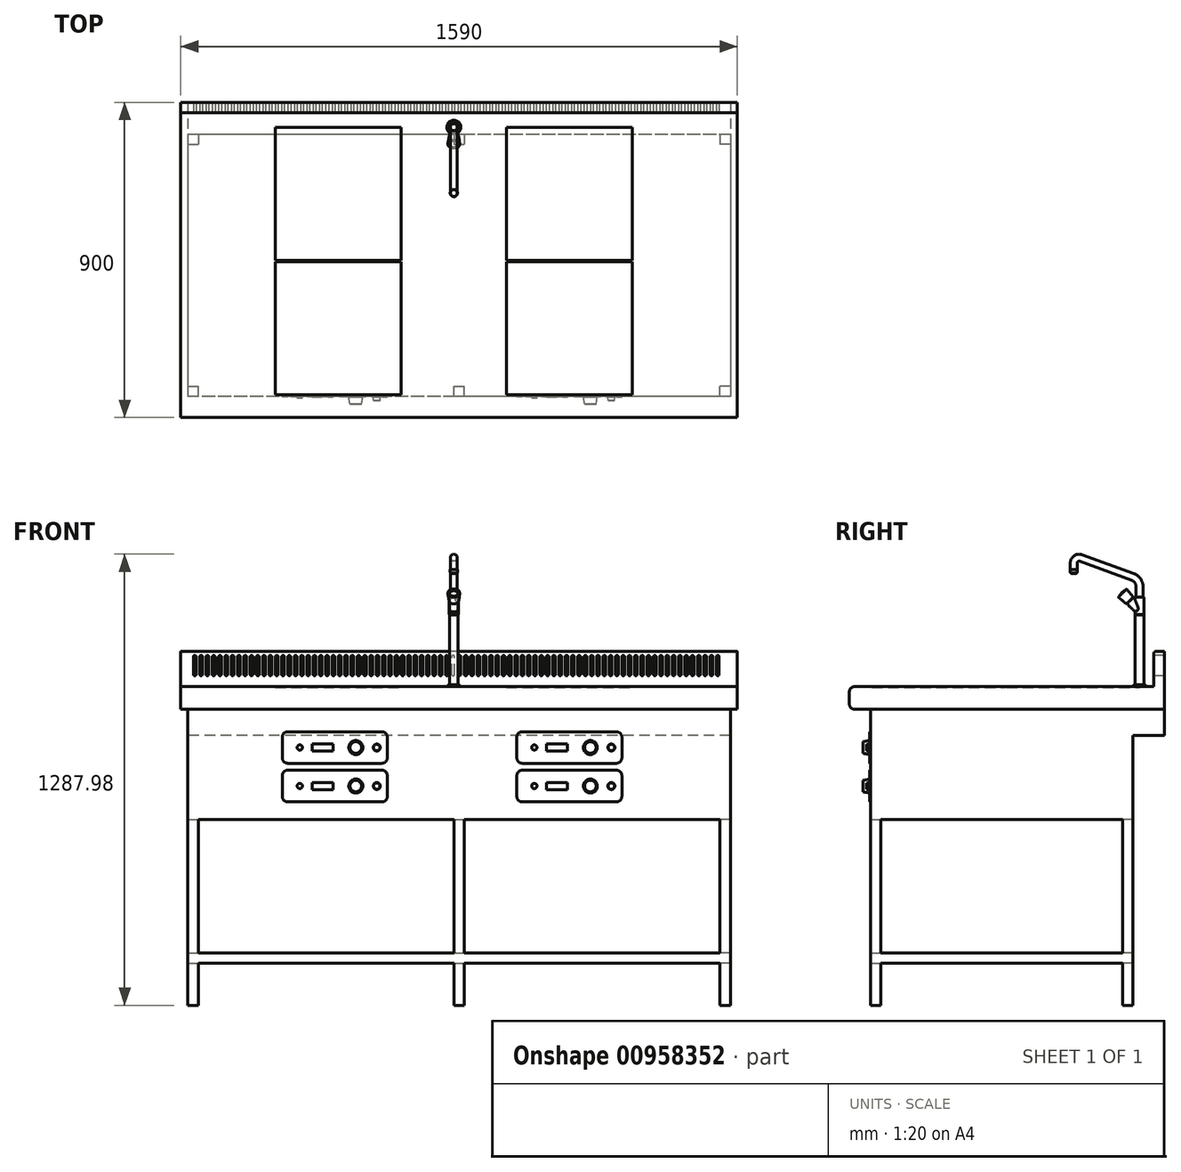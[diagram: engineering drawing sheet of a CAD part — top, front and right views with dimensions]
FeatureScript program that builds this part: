
annotation { "Feature Type Name" : "Feature", "Feature Type Description" : "" }
export const myFeature = defineFeature(function(context is Context, id is Id, definition is map)
    precondition{}
    {
        {
            var Q0;
            Q0=qCreatedBy(makeId("Right.planeOp"),FACE);
            var sketch = newSketch(context, id + "F0", { "sketchPlane" : qUnion([Q0])});
            skLineSegment(sketch, "E0", {"start": v(15, 0) * mm, "end": v(900, 0) * mm});
            skLineSegment(sketch, "E1", {"start": v(900, 0) * mm, "end": v(900, 165) * mm});
            skLineSegment(sketch, "E2", {"start": v(900, 165) * mm, "end": v(875, 165) * mm});
            skLineSegment(sketch, "E3", {"start": v(870, 160) * mm, "end": v(870, 65) * mm});
            skLineSegment(sketch, "E4", {"start": v(870, 65) * mm, "end": v(15, 65) * mm});
            skLineSegment(sketch, "E5", {"start": v(0, 50) * mm, "end": v(0, 15) * mm});
            skPoint(sketch, "E6.visualSharp", {"position": v(0, 65) * mm});
            skArc(sketch, "E6.filletArc", {"start": v(15, 65) * mm, "mid": v(4.4, 60.6) * mm, "end": v(0, 50) * mm});
            skPoint(sketch, "E7.visualSharp", {"position": v(0, 0) * mm});
            skArc(sketch, "E7.filletArc", {"start": v(0, 15) * mm, "mid": v(4.4, 4.4) * mm, "end": v(15, 0) * mm});
            skPoint(sketch, "E8.visualSharp", {"position": v(870, 165) * mm});
            skArc(sketch, "E8.filletArc", {"start": v(875, 165) * mm, "mid": v(871.46, 163.54) * mm, "end": v(870, 160) * mm});
            skPoint(sketch, "E9.visualSharp", {"position": v(900, 165) * mm});
            skSolve(sketch);
        }
        {
            var Q0;
            Q0 = qSketchRegion(id + "F0", true);
            extrude(context, id + "F1", {"entities" : qUnion([Q0]), "depth" : 1590 * mm, "offsetDistance" : 25 * mm});
        }
        {
            var Q0;
            Q0=makeQuery(id+"F1.opExtrude","SWEPT_FACE",FACE,{"disambiguationData":[OSD([sQuery(id+"F0.wireOp",EDGE,"E4")])]});
            var sketch = newSketch(context, id + "F2", { "sketchPlane" : qUnion([Q0])});
            skLineSegment(sketch, "E10.bottom", {"start": v(270, 65) * mm, "end": v(630, 65) * mm});
            skLineSegment(sketch, "E10.top", {"start": v(270, 445) * mm, "end": v(630, 445) * mm});
            skLineSegment(sketch, "E10.left", {"start": v(270, 65) * mm, "end": v(270, 445) * mm});
            skLineSegment(sketch, "E10.right", {"start": v(630, 65) * mm, "end": v(630, 445) * mm});
            skLineSegment(sketch, "E11.bottom", {"start": v(270, 449) * mm, "end": v(630, 449) * mm});
            skLineSegment(sketch, "E11.top", {"start": v(270, 829) * mm, "end": v(630, 829) * mm});
            skLineSegment(sketch, "E11.left", {"start": v(270, 449) * mm, "end": v(270, 829) * mm});
            skLineSegment(sketch, "E11.right", {"start": v(630, 449) * mm, "end": v(630, 829) * mm});
            skLineSegment(sketch, "E12.bottom", {"start": v(930, 65) * mm, "end": v(1290, 65) * mm});
            skLineSegment(sketch, "E12.top", {"start": v(930, 445) * mm, "end": v(1290, 445) * mm});
            skLineSegment(sketch, "E12.left", {"start": v(930, 65) * mm, "end": v(930, 445) * mm});
            skLineSegment(sketch, "E12.right", {"start": v(1290, 65) * mm, "end": v(1290, 445) * mm});
            skLineSegment(sketch, "E13.bottom", {"start": v(930, 449) * mm, "end": v(1290, 449) * mm});
            skLineSegment(sketch, "E13.top", {"start": v(930, 829) * mm, "end": v(1290, 829) * mm});
            skLineSegment(sketch, "E13.left", {"start": v(930, 449) * mm, "end": v(930, 829) * mm});
            skLineSegment(sketch, "E13.right", {"start": v(1290, 449) * mm, "end": v(1290, 829) * mm});
            skSolve(sketch);
        }
        {
            var Q0;
            Q0 = qSketchRegion(id + "F2", true);
            extrude(context, id + "F3", {"entities" : qUnion([Q0]), "operationType" : NewBodyOperationType.REMOVE, "oppositeDirection" : true, "depth" : 2 * mm, "offsetDistance" : 25 * mm});
        }
        {
            var Q0;
            Q0=makeQuery(id+"F1.opExtrude","SWEPT_FACE",FACE,{"disambiguationData":[OSD([sQuery(id+"F0.wireOp",EDGE,"E3")])]});
            var sketch = newSketch(context, id + "F4", { "sketchPlane" : qUnion([Q0])});
            skLineSegment(sketch, "E14", {"start": v(40, 150) * mm, "end": v(40, 100) * mm});
            skArc(sketch, "E15.0.startCap", {"start": v(36, 150) * mm, "mid": v(40, 154) * mm, "end": v(44, 150) * mm});
            skArc(sketch, "E15.0.endCap", {"start": v(44, 100) * mm, "mid": v(40, 96) * mm, "end": v(36, 100) * mm});
            skLineSegment(sketch, "E15.0.left", {"start": v(44, 150) * mm, "end": v(44, 100) * mm});
            skLineSegment(sketch, "E15.0.right", {"start": v(36, 150) * mm, "end": v(36, 100) * mm});
            skLineSegment(sketch, "E16.1.0.0", {"start": v(62, 150) * mm, "end": v(62, 100) * mm});
            skArc(sketch, "E16.1.0.1", {"start": v(54, 150) * mm, "mid": v(58, 154) * mm, "end": v(62, 150) * mm});
            skLineSegment(sketch, "E16.1.0.2", {"start": v(54, 150) * mm, "end": v(54, 100) * mm});
            skArc(sketch, "E16.1.0.3", {"start": v(62, 100) * mm, "mid": v(58, 96) * mm, "end": v(54, 100) * mm});
            skLineSegment(sketch, "E16.2.0.0", {"start": v(80, 150) * mm, "end": v(80, 100) * mm});
            skArc(sketch, "E16.2.0.1", {"start": v(72, 150) * mm, "mid": v(76, 154) * mm, "end": v(80, 150) * mm});
            skLineSegment(sketch, "E16.2.0.2", {"start": v(72, 150) * mm, "end": v(72, 100) * mm});
            skArc(sketch, "E16.2.0.3", {"start": v(80, 100) * mm, "mid": v(76, 96) * mm, "end": v(72, 100) * mm});
            skLineSegment(sketch, "E16.3.0.0", {"start": v(98, 150) * mm, "end": v(98, 100) * mm});
            skArc(sketch, "E16.3.0.1", {"start": v(90, 150) * mm, "mid": v(94, 154) * mm, "end": v(98, 150) * mm});
            skLineSegment(sketch, "E16.3.0.2", {"start": v(90, 150) * mm, "end": v(90, 100) * mm});
            skArc(sketch, "E16.3.0.3", {"start": v(98, 100) * mm, "mid": v(94, 96) * mm, "end": v(90, 100) * mm});
            skLineSegment(sketch, "E16.4.0.0", {"start": v(116, 150) * mm, "end": v(116, 100) * mm});
            skArc(sketch, "E16.4.0.1", {"start": v(108, 150) * mm, "mid": v(112, 154) * mm, "end": v(116, 150) * mm});
            skLineSegment(sketch, "E16.4.0.2", {"start": v(108, 150) * mm, "end": v(108, 100) * mm});
            skArc(sketch, "E16.4.0.3", {"start": v(116, 100) * mm, "mid": v(112, 96) * mm, "end": v(108, 100) * mm});
            skLineSegment(sketch, "E16.5.0.0", {"start": v(134, 150) * mm, "end": v(134, 100) * mm});
            skArc(sketch, "E16.5.0.1", {"start": v(126, 150) * mm, "mid": v(130, 154) * mm, "end": v(134, 150) * mm});
            skLineSegment(sketch, "E16.5.0.2", {"start": v(126, 150) * mm, "end": v(126, 100) * mm});
            skArc(sketch, "E16.5.0.3", {"start": v(134, 100) * mm, "mid": v(130, 96) * mm, "end": v(126, 100) * mm});
            skLineSegment(sketch, "E16.6.0.0", {"start": v(152, 150) * mm, "end": v(152, 100) * mm});
            skArc(sketch, "E16.6.0.1", {"start": v(144, 150) * mm, "mid": v(148, 154) * mm, "end": v(152, 150) * mm});
            skLineSegment(sketch, "E16.6.0.2", {"start": v(144, 150) * mm, "end": v(144, 100) * mm});
            skArc(sketch, "E16.6.0.3", {"start": v(152, 100) * mm, "mid": v(148, 96) * mm, "end": v(144, 100) * mm});
            skLineSegment(sketch, "E16.7.0.0", {"start": v(170, 150) * mm, "end": v(170, 100) * mm});
            skArc(sketch, "E16.7.0.1", {"start": v(162, 150) * mm, "mid": v(166, 154) * mm, "end": v(170, 150) * mm});
            skLineSegment(sketch, "E16.7.0.2", {"start": v(162, 150) * mm, "end": v(162, 100) * mm});
            skArc(sketch, "E16.7.0.3", {"start": v(170, 100) * mm, "mid": v(166, 96) * mm, "end": v(162, 100) * mm});
            skLineSegment(sketch, "E16.8.0.0", {"start": v(188, 150) * mm, "end": v(188, 100) * mm});
            skArc(sketch, "E16.8.0.1", {"start": v(180, 150) * mm, "mid": v(184, 154) * mm, "end": v(188, 150) * mm});
            skLineSegment(sketch, "E16.8.0.2", {"start": v(180, 150) * mm, "end": v(180, 100) * mm});
            skArc(sketch, "E16.8.0.3", {"start": v(188, 100) * mm, "mid": v(184, 96) * mm, "end": v(180, 100) * mm});
            skLineSegment(sketch, "E16.9.0.0", {"start": v(206, 150) * mm, "end": v(206, 100) * mm});
            skArc(sketch, "E16.9.0.1", {"start": v(198, 150) * mm, "mid": v(202, 154) * mm, "end": v(206, 150) * mm});
            skLineSegment(sketch, "E16.9.0.2", {"start": v(198, 150) * mm, "end": v(198, 100) * mm});
            skArc(sketch, "E16.9.0.3", {"start": v(206, 100) * mm, "mid": v(202, 96) * mm, "end": v(198, 100) * mm});
            skLineSegment(sketch, "E16.10.0.0", {"start": v(224, 150) * mm, "end": v(224, 100) * mm});
            skArc(sketch, "E16.10.0.1", {"start": v(216, 150) * mm, "mid": v(220, 154) * mm, "end": v(224, 150) * mm});
            skLineSegment(sketch, "E16.10.0.2", {"start": v(216, 150) * mm, "end": v(216, 100) * mm});
            skArc(sketch, "E16.10.0.3", {"start": v(224, 100) * mm, "mid": v(220, 96) * mm, "end": v(216, 100) * mm});
            skLineSegment(sketch, "E16.11.0.0", {"start": v(242, 150) * mm, "end": v(242, 100) * mm});
            skArc(sketch, "E16.11.0.1", {"start": v(234, 150) * mm, "mid": v(238, 154) * mm, "end": v(242, 150) * mm});
            skLineSegment(sketch, "E16.11.0.2", {"start": v(234, 150) * mm, "end": v(234, 100) * mm});
            skArc(sketch, "E16.11.0.3", {"start": v(242, 100) * mm, "mid": v(238, 96) * mm, "end": v(234, 100) * mm});
            skLineSegment(sketch, "E16.12.0.0", {"start": v(260, 150) * mm, "end": v(260, 100) * mm});
            skArc(sketch, "E16.12.0.1", {"start": v(252, 150) * mm, "mid": v(256, 154) * mm, "end": v(260, 150) * mm});
            skLineSegment(sketch, "E16.12.0.2", {"start": v(252, 150) * mm, "end": v(252, 100) * mm});
            skArc(sketch, "E16.12.0.3", {"start": v(260, 100) * mm, "mid": v(256, 96) * mm, "end": v(252, 100) * mm});
            skLineSegment(sketch, "E16.13.0.0", {"start": v(278, 150) * mm, "end": v(278, 100) * mm});
            skArc(sketch, "E16.13.0.1", {"start": v(270, 150) * mm, "mid": v(274, 154) * mm, "end": v(278, 150) * mm});
            skLineSegment(sketch, "E16.13.0.2", {"start": v(270, 150) * mm, "end": v(270, 100) * mm});
            skArc(sketch, "E16.13.0.3", {"start": v(278, 100) * mm, "mid": v(274, 96) * mm, "end": v(270, 100) * mm});
            skLineSegment(sketch, "E16.14.0.0", {"start": v(296, 150) * mm, "end": v(296, 100) * mm});
            skArc(sketch, "E16.14.0.1", {"start": v(288, 150) * mm, "mid": v(292, 154) * mm, "end": v(296, 150) * mm});
            skLineSegment(sketch, "E16.14.0.2", {"start": v(288, 150) * mm, "end": v(288, 100) * mm});
            skArc(sketch, "E16.14.0.3", {"start": v(296, 100) * mm, "mid": v(292, 96) * mm, "end": v(288, 100) * mm});
            skLineSegment(sketch, "E16.15.0.0", {"start": v(314, 150) * mm, "end": v(314, 100) * mm});
            skArc(sketch, "E16.15.0.1", {"start": v(306, 150) * mm, "mid": v(310, 154) * mm, "end": v(314, 150) * mm});
            skLineSegment(sketch, "E16.15.0.2", {"start": v(306, 150) * mm, "end": v(306, 100) * mm});
            skArc(sketch, "E16.15.0.3", {"start": v(314, 100) * mm, "mid": v(310, 96) * mm, "end": v(306, 100) * mm});
            skLineSegment(sketch, "E16.16.0.0", {"start": v(332, 150) * mm, "end": v(332, 100) * mm});
            skArc(sketch, "E16.16.0.1", {"start": v(324, 150) * mm, "mid": v(328, 154) * mm, "end": v(332, 150) * mm});
            skLineSegment(sketch, "E16.16.0.2", {"start": v(324, 150) * mm, "end": v(324, 100) * mm});
            skArc(sketch, "E16.16.0.3", {"start": v(332, 100) * mm, "mid": v(328, 96) * mm, "end": v(324, 100) * mm});
            skLineSegment(sketch, "E16.17.0.0", {"start": v(350, 150) * mm, "end": v(350, 100) * mm});
            skArc(sketch, "E16.17.0.1", {"start": v(342, 150) * mm, "mid": v(346, 154) * mm, "end": v(350, 150) * mm});
            skLineSegment(sketch, "E16.17.0.2", {"start": v(342, 150) * mm, "end": v(342, 100) * mm});
            skArc(sketch, "E16.17.0.3", {"start": v(350, 100) * mm, "mid": v(346, 96) * mm, "end": v(342, 100) * mm});
            skLineSegment(sketch, "E16.18.0.0", {"start": v(368, 150) * mm, "end": v(368, 100) * mm});
            skArc(sketch, "E16.18.0.1", {"start": v(360, 150) * mm, "mid": v(364, 154) * mm, "end": v(368, 150) * mm});
            skLineSegment(sketch, "E16.18.0.2", {"start": v(360, 150) * mm, "end": v(360, 100) * mm});
            skArc(sketch, "E16.18.0.3", {"start": v(368, 100) * mm, "mid": v(364, 96) * mm, "end": v(360, 100) * mm});
            skLineSegment(sketch, "E16.19.0.0", {"start": v(386, 150) * mm, "end": v(386, 100) * mm});
            skArc(sketch, "E16.19.0.1", {"start": v(378, 150) * mm, "mid": v(382, 154) * mm, "end": v(386, 150) * mm});
            skLineSegment(sketch, "E16.19.0.2", {"start": v(378, 150) * mm, "end": v(378, 100) * mm});
            skArc(sketch, "E16.19.0.3", {"start": v(386, 100) * mm, "mid": v(382, 96) * mm, "end": v(378, 100) * mm});
            skLineSegment(sketch, "E16.20.0.0", {"start": v(404, 150) * mm, "end": v(404, 100) * mm});
            skArc(sketch, "E16.20.0.1", {"start": v(396, 150) * mm, "mid": v(400, 154) * mm, "end": v(404, 150) * mm});
            skLineSegment(sketch, "E16.20.0.2", {"start": v(396, 150) * mm, "end": v(396, 100) * mm});
            skArc(sketch, "E16.20.0.3", {"start": v(404, 100) * mm, "mid": v(400, 96) * mm, "end": v(396, 100) * mm});
            skLineSegment(sketch, "E16.21.0.0", {"start": v(422, 150) * mm, "end": v(422, 100) * mm});
            skArc(sketch, "E16.21.0.1", {"start": v(414, 150) * mm, "mid": v(418, 154) * mm, "end": v(422, 150) * mm});
            skLineSegment(sketch, "E16.21.0.2", {"start": v(414, 150) * mm, "end": v(414, 100) * mm});
            skArc(sketch, "E16.21.0.3", {"start": v(422, 100) * mm, "mid": v(418, 96) * mm, "end": v(414, 100) * mm});
            skLineSegment(sketch, "E16.22.0.0", {"start": v(440, 150) * mm, "end": v(440, 100) * mm});
            skArc(sketch, "E16.22.0.1", {"start": v(432, 150) * mm, "mid": v(436, 154) * mm, "end": v(440, 150) * mm});
            skLineSegment(sketch, "E16.22.0.2", {"start": v(432, 150) * mm, "end": v(432, 100) * mm});
            skArc(sketch, "E16.22.0.3", {"start": v(440, 100) * mm, "mid": v(436, 96) * mm, "end": v(432, 100) * mm});
            skLineSegment(sketch, "E16.23.0.0", {"start": v(458, 150) * mm, "end": v(458, 100) * mm});
            skArc(sketch, "E16.23.0.1", {"start": v(450, 150) * mm, "mid": v(454, 154) * mm, "end": v(458, 150) * mm});
            skLineSegment(sketch, "E16.23.0.2", {"start": v(450, 150) * mm, "end": v(450, 100) * mm});
            skArc(sketch, "E16.23.0.3", {"start": v(458, 100) * mm, "mid": v(454, 96) * mm, "end": v(450, 100) * mm});
            skLineSegment(sketch, "E16.24.0.0", {"start": v(476, 150) * mm, "end": v(476, 100) * mm});
            skArc(sketch, "E16.24.0.1", {"start": v(468, 150) * mm, "mid": v(472, 154) * mm, "end": v(476, 150) * mm});
            skLineSegment(sketch, "E16.24.0.2", {"start": v(468, 150) * mm, "end": v(468, 100) * mm});
            skArc(sketch, "E16.24.0.3", {"start": v(476, 100) * mm, "mid": v(472, 96) * mm, "end": v(468, 100) * mm});
            skLineSegment(sketch, "E16.25.0.0", {"start": v(494, 150) * mm, "end": v(494, 100) * mm});
            skArc(sketch, "E16.25.0.1", {"start": v(486, 150) * mm, "mid": v(490, 154) * mm, "end": v(494, 150) * mm});
            skLineSegment(sketch, "E16.25.0.2", {"start": v(486, 150) * mm, "end": v(486, 100) * mm});
            skArc(sketch, "E16.25.0.3", {"start": v(494, 100) * mm, "mid": v(490, 96) * mm, "end": v(486, 100) * mm});
            skLineSegment(sketch, "E16.26.0.0", {"start": v(512, 150) * mm, "end": v(512, 100) * mm});
            skArc(sketch, "E16.26.0.1", {"start": v(504, 150) * mm, "mid": v(508, 154) * mm, "end": v(512, 150) * mm});
            skLineSegment(sketch, "E16.26.0.2", {"start": v(504, 150) * mm, "end": v(504, 100) * mm});
            skArc(sketch, "E16.26.0.3", {"start": v(512, 100) * mm, "mid": v(508, 96) * mm, "end": v(504, 100) * mm});
            skLineSegment(sketch, "E16.27.0.0", {"start": v(530, 150) * mm, "end": v(530, 100) * mm});
            skArc(sketch, "E16.27.0.1", {"start": v(522, 150) * mm, "mid": v(526, 154) * mm, "end": v(530, 150) * mm});
            skLineSegment(sketch, "E16.27.0.2", {"start": v(522, 150) * mm, "end": v(522, 100) * mm});
            skArc(sketch, "E16.27.0.3", {"start": v(530, 100) * mm, "mid": v(526, 96) * mm, "end": v(522, 100) * mm});
            skLineSegment(sketch, "E16.28.0.0", {"start": v(548, 150) * mm, "end": v(548, 100) * mm});
            skArc(sketch, "E16.28.0.1", {"start": v(540, 150) * mm, "mid": v(544, 154) * mm, "end": v(548, 150) * mm});
            skLineSegment(sketch, "E16.28.0.2", {"start": v(540, 150) * mm, "end": v(540, 100) * mm});
            skArc(sketch, "E16.28.0.3", {"start": v(548, 100) * mm, "mid": v(544, 96) * mm, "end": v(540, 100) * mm});
            skLineSegment(sketch, "E16.29.0.0", {"start": v(566, 150) * mm, "end": v(566, 100) * mm});
            skArc(sketch, "E16.29.0.1", {"start": v(558, 150) * mm, "mid": v(562, 154) * mm, "end": v(566, 150) * mm});
            skLineSegment(sketch, "E16.29.0.2", {"start": v(558, 150) * mm, "end": v(558, 100) * mm});
            skArc(sketch, "E16.29.0.3", {"start": v(566, 100) * mm, "mid": v(562, 96) * mm, "end": v(558, 100) * mm});
            skLineSegment(sketch, "E16.30.0.0", {"start": v(584, 150) * mm, "end": v(584, 100) * mm});
            skArc(sketch, "E16.30.0.1", {"start": v(576, 150) * mm, "mid": v(580, 154) * mm, "end": v(584, 150) * mm});
            skLineSegment(sketch, "E16.30.0.2", {"start": v(576, 150) * mm, "end": v(576, 100) * mm});
            skArc(sketch, "E16.30.0.3", {"start": v(584, 100) * mm, "mid": v(580, 96) * mm, "end": v(576, 100) * mm});
            skLineSegment(sketch, "E16.31.0.0", {"start": v(602, 150) * mm, "end": v(602, 100) * mm});
            skArc(sketch, "E16.31.0.1", {"start": v(594, 150) * mm, "mid": v(598, 154) * mm, "end": v(602, 150) * mm});
            skLineSegment(sketch, "E16.31.0.2", {"start": v(594, 150) * mm, "end": v(594, 100) * mm});
            skArc(sketch, "E16.31.0.3", {"start": v(602, 100) * mm, "mid": v(598, 96) * mm, "end": v(594, 100) * mm});
            skLineSegment(sketch, "E16.32.0.0", {"start": v(620, 150) * mm, "end": v(620, 100) * mm});
            skArc(sketch, "E16.32.0.1", {"start": v(612, 150) * mm, "mid": v(616, 154) * mm, "end": v(620, 150) * mm});
            skLineSegment(sketch, "E16.32.0.2", {"start": v(612, 150) * mm, "end": v(612, 100) * mm});
            skArc(sketch, "E16.32.0.3", {"start": v(620, 100) * mm, "mid": v(616, 96) * mm, "end": v(612, 100) * mm});
            skLineSegment(sketch, "E16.33.0.0", {"start": v(638, 150) * mm, "end": v(638, 100) * mm});
            skArc(sketch, "E16.33.0.1", {"start": v(630, 150) * mm, "mid": v(634, 154) * mm, "end": v(638, 150) * mm});
            skLineSegment(sketch, "E16.33.0.2", {"start": v(630, 150) * mm, "end": v(630, 100) * mm});
            skArc(sketch, "E16.33.0.3", {"start": v(638, 100) * mm, "mid": v(634, 96) * mm, "end": v(630, 100) * mm});
            skLineSegment(sketch, "E16.34.0.0", {"start": v(656, 150) * mm, "end": v(656, 100) * mm});
            skArc(sketch, "E16.34.0.1", {"start": v(648, 150) * mm, "mid": v(652, 154) * mm, "end": v(656, 150) * mm});
            skLineSegment(sketch, "E16.34.0.2", {"start": v(648, 150) * mm, "end": v(648, 100) * mm});
            skArc(sketch, "E16.34.0.3", {"start": v(656, 100) * mm, "mid": v(652, 96) * mm, "end": v(648, 100) * mm});
            skLineSegment(sketch, "E16.35.0.0", {"start": v(674, 150) * mm, "end": v(674, 100) * mm});
            skArc(sketch, "E16.35.0.1", {"start": v(666, 150) * mm, "mid": v(670, 154) * mm, "end": v(674, 150) * mm});
            skLineSegment(sketch, "E16.35.0.2", {"start": v(666, 150) * mm, "end": v(666, 100) * mm});
            skArc(sketch, "E16.35.0.3", {"start": v(674, 100) * mm, "mid": v(670, 96) * mm, "end": v(666, 100) * mm});
            skLineSegment(sketch, "E16.36.0.0", {"start": v(692, 150) * mm, "end": v(692, 100) * mm});
            skArc(sketch, "E16.36.0.1", {"start": v(684, 150) * mm, "mid": v(688, 154) * mm, "end": v(692, 150) * mm});
            skLineSegment(sketch, "E16.36.0.2", {"start": v(684, 150) * mm, "end": v(684, 100) * mm});
            skArc(sketch, "E16.36.0.3", {"start": v(692, 100) * mm, "mid": v(688, 96) * mm, "end": v(684, 100) * mm});
            skLineSegment(sketch, "E16.37.0.0", {"start": v(710, 150) * mm, "end": v(710, 100) * mm});
            skArc(sketch, "E16.37.0.1", {"start": v(702, 150) * mm, "mid": v(706, 154) * mm, "end": v(710, 150) * mm});
            skLineSegment(sketch, "E16.37.0.2", {"start": v(702, 150) * mm, "end": v(702, 100) * mm});
            skArc(sketch, "E16.37.0.3", {"start": v(710, 100) * mm, "mid": v(706, 96) * mm, "end": v(702, 100) * mm});
            skLineSegment(sketch, "E16.38.0.0", {"start": v(728, 150) * mm, "end": v(728, 100) * mm});
            skArc(sketch, "E16.38.0.1", {"start": v(720, 150) * mm, "mid": v(724, 154) * mm, "end": v(728, 150) * mm});
            skLineSegment(sketch, "E16.38.0.2", {"start": v(720, 150) * mm, "end": v(720, 100) * mm});
            skArc(sketch, "E16.38.0.3", {"start": v(728, 100) * mm, "mid": v(724, 96) * mm, "end": v(720, 100) * mm});
            skLineSegment(sketch, "E16.39.0.0", {"start": v(746, 150) * mm, "end": v(746, 100) * mm});
            skArc(sketch, "E16.39.0.1", {"start": v(738, 150) * mm, "mid": v(742, 154) * mm, "end": v(746, 150) * mm});
            skLineSegment(sketch, "E16.39.0.2", {"start": v(738, 150) * mm, "end": v(738, 100) * mm});
            skArc(sketch, "E16.39.0.3", {"start": v(746, 100) * mm, "mid": v(742, 96) * mm, "end": v(738, 100) * mm});
            skLineSegment(sketch, "E16.40.0.0", {"start": v(764, 150) * mm, "end": v(764, 100) * mm});
            skArc(sketch, "E16.40.0.1", {"start": v(756, 150) * mm, "mid": v(760, 154) * mm, "end": v(764, 150) * mm});
            skLineSegment(sketch, "E16.40.0.2", {"start": v(756, 150) * mm, "end": v(756, 100) * mm});
            skArc(sketch, "E16.40.0.3", {"start": v(764, 100) * mm, "mid": v(760, 96) * mm, "end": v(756, 100) * mm});
            skLineSegment(sketch, "E16.41.0.0", {"start": v(782, 150) * mm, "end": v(782, 100) * mm});
            skArc(sketch, "E16.41.0.1", {"start": v(774, 150) * mm, "mid": v(778, 154) * mm, "end": v(782, 150) * mm});
            skLineSegment(sketch, "E16.41.0.2", {"start": v(774, 150) * mm, "end": v(774, 100) * mm});
            skArc(sketch, "E16.41.0.3", {"start": v(782, 100) * mm, "mid": v(778, 96) * mm, "end": v(774, 100) * mm});
            skLineSegment(sketch, "E16.42.0.0", {"start": v(800, 150) * mm, "end": v(800, 100) * mm});
            skArc(sketch, "E16.42.0.1", {"start": v(792, 150) * mm, "mid": v(796, 154) * mm, "end": v(800, 150) * mm});
            skLineSegment(sketch, "E16.42.0.2", {"start": v(792, 150) * mm, "end": v(792, 100) * mm});
            skArc(sketch, "E16.42.0.3", {"start": v(800, 100) * mm, "mid": v(796, 96) * mm, "end": v(792, 100) * mm});
            skLineSegment(sketch, "E16.43.0.0", {"start": v(818, 150) * mm, "end": v(818, 100) * mm});
            skArc(sketch, "E16.43.0.1", {"start": v(810, 150) * mm, "mid": v(814, 154) * mm, "end": v(818, 150) * mm});
            skLineSegment(sketch, "E16.43.0.2", {"start": v(810, 150) * mm, "end": v(810, 100) * mm});
            skArc(sketch, "E16.43.0.3", {"start": v(818, 100) * mm, "mid": v(814, 96) * mm, "end": v(810, 100) * mm});
            skLineSegment(sketch, "E16.44.0.0", {"start": v(836, 150) * mm, "end": v(836, 100) * mm});
            skArc(sketch, "E16.44.0.1", {"start": v(828, 150) * mm, "mid": v(832, 154) * mm, "end": v(836, 150) * mm});
            skLineSegment(sketch, "E16.44.0.2", {"start": v(828, 150) * mm, "end": v(828, 100) * mm});
            skArc(sketch, "E16.44.0.3", {"start": v(836, 100) * mm, "mid": v(832, 96) * mm, "end": v(828, 100) * mm});
            skLineSegment(sketch, "E16.45.0.0", {"start": v(854, 150) * mm, "end": v(854, 100) * mm});
            skArc(sketch, "E16.45.0.1", {"start": v(846, 150) * mm, "mid": v(850, 154) * mm, "end": v(854, 150) * mm});
            skLineSegment(sketch, "E16.45.0.2", {"start": v(846, 150) * mm, "end": v(846, 100) * mm});
            skArc(sketch, "E16.45.0.3", {"start": v(854, 100) * mm, "mid": v(850, 96) * mm, "end": v(846, 100) * mm});
            skLineSegment(sketch, "E16.46.0.0", {"start": v(872, 150) * mm, "end": v(872, 100) * mm});
            skArc(sketch, "E16.46.0.1", {"start": v(864, 150) * mm, "mid": v(868, 154) * mm, "end": v(872, 150) * mm});
            skLineSegment(sketch, "E16.46.0.2", {"start": v(864, 150) * mm, "end": v(864, 100) * mm});
            skArc(sketch, "E16.46.0.3", {"start": v(872, 100) * mm, "mid": v(868, 96) * mm, "end": v(864, 100) * mm});
            skLineSegment(sketch, "E16.47.0.0", {"start": v(890, 150) * mm, "end": v(890, 100) * mm});
            skArc(sketch, "E16.47.0.1", {"start": v(882, 150) * mm, "mid": v(886, 154) * mm, "end": v(890, 150) * mm});
            skLineSegment(sketch, "E16.47.0.2", {"start": v(882, 150) * mm, "end": v(882, 100) * mm});
            skArc(sketch, "E16.47.0.3", {"start": v(890, 100) * mm, "mid": v(886, 96) * mm, "end": v(882, 100) * mm});
            skLineSegment(sketch, "E16.48.0.0", {"start": v(908, 150) * mm, "end": v(908, 100) * mm});
            skArc(sketch, "E16.48.0.1", {"start": v(900, 150) * mm, "mid": v(904, 154) * mm, "end": v(908, 150) * mm});
            skLineSegment(sketch, "E16.48.0.2", {"start": v(900, 150) * mm, "end": v(900, 100) * mm});
            skArc(sketch, "E16.48.0.3", {"start": v(908, 100) * mm, "mid": v(904, 96) * mm, "end": v(900, 100) * mm});
            skLineSegment(sketch, "E16.49.0.0", {"start": v(926, 150) * mm, "end": v(926, 100) * mm});
            skArc(sketch, "E16.49.0.1", {"start": v(918, 150) * mm, "mid": v(922, 154) * mm, "end": v(926, 150) * mm});
            skLineSegment(sketch, "E16.49.0.2", {"start": v(918, 150) * mm, "end": v(918, 100) * mm});
            skArc(sketch, "E16.49.0.3", {"start": v(926, 100) * mm, "mid": v(922, 96) * mm, "end": v(918, 100) * mm});
            skLineSegment(sketch, "E16.50.0.0", {"start": v(944, 150) * mm, "end": v(944, 100) * mm});
            skArc(sketch, "E16.50.0.1", {"start": v(936, 150) * mm, "mid": v(940, 154) * mm, "end": v(944, 150) * mm});
            skLineSegment(sketch, "E16.50.0.2", {"start": v(936, 150) * mm, "end": v(936, 100) * mm});
            skArc(sketch, "E16.50.0.3", {"start": v(944, 100) * mm, "mid": v(940, 96) * mm, "end": v(936, 100) * mm});
            skLineSegment(sketch, "E16.51.0.0", {"start": v(962, 150) * mm, "end": v(962, 100) * mm});
            skArc(sketch, "E16.51.0.1", {"start": v(954, 150) * mm, "mid": v(958, 154) * mm, "end": v(962, 150) * mm});
            skLineSegment(sketch, "E16.51.0.2", {"start": v(954, 150) * mm, "end": v(954, 100) * mm});
            skArc(sketch, "E16.51.0.3", {"start": v(962, 100) * mm, "mid": v(958, 96) * mm, "end": v(954, 100) * mm});
            skLineSegment(sketch, "E16.52.0.0", {"start": v(980, 150) * mm, "end": v(980, 100) * mm});
            skArc(sketch, "E16.52.0.1", {"start": v(972, 150) * mm, "mid": v(976, 154) * mm, "end": v(980, 150) * mm});
            skLineSegment(sketch, "E16.52.0.2", {"start": v(972, 150) * mm, "end": v(972, 100) * mm});
            skArc(sketch, "E16.52.0.3", {"start": v(980, 100) * mm, "mid": v(976, 96) * mm, "end": v(972, 100) * mm});
            skLineSegment(sketch, "E16.53.0.0", {"start": v(998, 150) * mm, "end": v(998, 100) * mm});
            skArc(sketch, "E16.53.0.1", {"start": v(990, 150) * mm, "mid": v(994, 154) * mm, "end": v(998, 150) * mm});
            skLineSegment(sketch, "E16.53.0.2", {"start": v(990, 150) * mm, "end": v(990, 100) * mm});
            skArc(sketch, "E16.53.0.3", {"start": v(998, 100) * mm, "mid": v(994, 96) * mm, "end": v(990, 100) * mm});
            skLineSegment(sketch, "E16.54.0.0", {"start": v(1016, 150) * mm, "end": v(1016, 100) * mm});
            skArc(sketch, "E16.54.0.1", {"start": v(1008, 150) * mm, "mid": v(1012, 154) * mm, "end": v(1016, 150) * mm});
            skLineSegment(sketch, "E16.54.0.2", {"start": v(1008, 150) * mm, "end": v(1008, 100) * mm});
            skArc(sketch, "E16.54.0.3", {"start": v(1016, 100) * mm, "mid": v(1012, 96) * mm, "end": v(1008, 100) * mm});
            skLineSegment(sketch, "E16.55.0.0", {"start": v(1034, 150) * mm, "end": v(1034, 100) * mm});
            skArc(sketch, "E16.55.0.1", {"start": v(1026, 150) * mm, "mid": v(1030, 154) * mm, "end": v(1034, 150) * mm});
            skLineSegment(sketch, "E16.55.0.2", {"start": v(1026, 150) * mm, "end": v(1026, 100) * mm});
            skArc(sketch, "E16.55.0.3", {"start": v(1034, 100) * mm, "mid": v(1030, 96) * mm, "end": v(1026, 100) * mm});
            skLineSegment(sketch, "E16.56.0.0", {"start": v(1052, 150) * mm, "end": v(1052, 100) * mm});
            skArc(sketch, "E16.56.0.1", {"start": v(1044, 150) * mm, "mid": v(1048, 154) * mm, "end": v(1052, 150) * mm});
            skLineSegment(sketch, "E16.56.0.2", {"start": v(1044, 150) * mm, "end": v(1044, 100) * mm});
            skArc(sketch, "E16.56.0.3", {"start": v(1052, 100) * mm, "mid": v(1048, 96) * mm, "end": v(1044, 100) * mm});
            skLineSegment(sketch, "E16.57.0.0", {"start": v(1070, 150) * mm, "end": v(1070, 100) * mm});
            skArc(sketch, "E16.57.0.1", {"start": v(1062, 150) * mm, "mid": v(1066, 154) * mm, "end": v(1070, 150) * mm});
            skLineSegment(sketch, "E16.57.0.2", {"start": v(1062, 150) * mm, "end": v(1062, 100) * mm});
            skArc(sketch, "E16.57.0.3", {"start": v(1070, 100) * mm, "mid": v(1066, 96) * mm, "end": v(1062, 100) * mm});
            skLineSegment(sketch, "E16.58.0.0", {"start": v(1088, 150) * mm, "end": v(1088, 100) * mm});
            skArc(sketch, "E16.58.0.1", {"start": v(1080, 150) * mm, "mid": v(1084, 154) * mm, "end": v(1088, 150) * mm});
            skLineSegment(sketch, "E16.58.0.2", {"start": v(1080, 150) * mm, "end": v(1080, 100) * mm});
            skArc(sketch, "E16.58.0.3", {"start": v(1088, 100) * mm, "mid": v(1084, 96) * mm, "end": v(1080, 100) * mm});
            skLineSegment(sketch, "E16.59.0.0", {"start": v(1106, 150) * mm, "end": v(1106, 100) * mm});
            skArc(sketch, "E16.59.0.1", {"start": v(1098, 150) * mm, "mid": v(1102, 154) * mm, "end": v(1106, 150) * mm});
            skLineSegment(sketch, "E16.59.0.2", {"start": v(1098, 150) * mm, "end": v(1098, 100) * mm});
            skArc(sketch, "E16.59.0.3", {"start": v(1106, 100) * mm, "mid": v(1102, 96) * mm, "end": v(1098, 100) * mm});
            skLineSegment(sketch, "E16.direction1", {"start": v(44, 100) * mm, "end": v(62, 100) * mm, "construction": true});
            skLineSegment(sketch, "E17.0.60.0", {"start": v(1124, 150) * mm, "end": v(1124, 100) * mm});
            skArc(sketch, "E17.3.60.0", {"start": v(1116, 150) * mm, "mid": v(1120, 154) * mm, "end": v(1124, 150) * mm});
            skLineSegment(sketch, "E17.7.60.0", {"start": v(1116, 150) * mm, "end": v(1116, 100) * mm});
            skArc(sketch, "E17.10.60.0", {"start": v(1124, 100) * mm, "mid": v(1120, 96) * mm, "end": v(1116, 100) * mm});
            skLineSegment(sketch, "E17.0.61.0", {"start": v(1142, 150) * mm, "end": v(1142, 100) * mm});
            skArc(sketch, "E17.3.61.0", {"start": v(1134, 150) * mm, "mid": v(1138, 154) * mm, "end": v(1142, 150) * mm});
            skLineSegment(sketch, "E17.7.61.0", {"start": v(1134, 150) * mm, "end": v(1134, 100) * mm});
            skArc(sketch, "E17.10.61.0", {"start": v(1142, 100) * mm, "mid": v(1138, 96) * mm, "end": v(1134, 100) * mm});
            skLineSegment(sketch, "E17.0.62.0", {"start": v(1160, 150) * mm, "end": v(1160, 100) * mm});
            skArc(sketch, "E17.3.62.0", {"start": v(1152, 150) * mm, "mid": v(1156, 154) * mm, "end": v(1160, 150) * mm});
            skLineSegment(sketch, "E17.7.62.0", {"start": v(1152, 150) * mm, "end": v(1152, 100) * mm});
            skArc(sketch, "E17.10.62.0", {"start": v(1160, 100) * mm, "mid": v(1156, 96) * mm, "end": v(1152, 100) * mm});
            skLineSegment(sketch, "E17.0.63.0", {"start": v(1178, 150) * mm, "end": v(1178, 100) * mm});
            skArc(sketch, "E17.3.63.0", {"start": v(1170, 150) * mm, "mid": v(1174, 154) * mm, "end": v(1178, 150) * mm});
            skLineSegment(sketch, "E17.7.63.0", {"start": v(1170, 150) * mm, "end": v(1170, 100) * mm});
            skArc(sketch, "E17.10.63.0", {"start": v(1178, 100) * mm, "mid": v(1174, 96) * mm, "end": v(1170, 100) * mm});
            skLineSegment(sketch, "E17.0.64.0", {"start": v(1196, 150) * mm, "end": v(1196, 100) * mm});
            skArc(sketch, "E17.3.64.0", {"start": v(1188, 150) * mm, "mid": v(1192, 154) * mm, "end": v(1196, 150) * mm});
            skLineSegment(sketch, "E17.7.64.0", {"start": v(1188, 150) * mm, "end": v(1188, 100) * mm});
            skArc(sketch, "E17.10.64.0", {"start": v(1196, 100) * mm, "mid": v(1192, 96) * mm, "end": v(1188, 100) * mm});
            skLineSegment(sketch, "E17.0.65.0", {"start": v(1214, 150) * mm, "end": v(1214, 100) * mm});
            skArc(sketch, "E17.3.65.0", {"start": v(1206, 150) * mm, "mid": v(1210, 154) * mm, "end": v(1214, 150) * mm});
            skLineSegment(sketch, "E17.7.65.0", {"start": v(1206, 150) * mm, "end": v(1206, 100) * mm});
            skArc(sketch, "E17.10.65.0", {"start": v(1214, 100) * mm, "mid": v(1210, 96) * mm, "end": v(1206, 100) * mm});
            skLineSegment(sketch, "E17.0.66.0", {"start": v(1232, 150) * mm, "end": v(1232, 100) * mm});
            skArc(sketch, "E17.3.66.0", {"start": v(1224, 150) * mm, "mid": v(1228, 154) * mm, "end": v(1232, 150) * mm});
            skLineSegment(sketch, "E17.7.66.0", {"start": v(1224, 150) * mm, "end": v(1224, 100) * mm});
            skArc(sketch, "E17.10.66.0", {"start": v(1232, 100) * mm, "mid": v(1228, 96) * mm, "end": v(1224, 100) * mm});
            skLineSegment(sketch, "E17.0.67.0", {"start": v(1250, 150) * mm, "end": v(1250, 100) * mm});
            skArc(sketch, "E17.3.67.0", {"start": v(1242, 150) * mm, "mid": v(1246, 154) * mm, "end": v(1250, 150) * mm});
            skLineSegment(sketch, "E17.7.67.0", {"start": v(1242, 150) * mm, "end": v(1242, 100) * mm});
            skArc(sketch, "E17.10.67.0", {"start": v(1250, 100) * mm, "mid": v(1246, 96) * mm, "end": v(1242, 100) * mm});
            skLineSegment(sketch, "E17.0.68.0", {"start": v(1268, 150) * mm, "end": v(1268, 100) * mm});
            skArc(sketch, "E17.3.68.0", {"start": v(1260, 150) * mm, "mid": v(1264, 154) * mm, "end": v(1268, 150) * mm});
            skLineSegment(sketch, "E17.7.68.0", {"start": v(1260, 150) * mm, "end": v(1260, 100) * mm});
            skArc(sketch, "E17.10.68.0", {"start": v(1268, 100) * mm, "mid": v(1264, 96) * mm, "end": v(1260, 100) * mm});
            skLineSegment(sketch, "E17.0.69.0", {"start": v(1286, 150) * mm, "end": v(1286, 100) * mm});
            skArc(sketch, "E17.3.69.0", {"start": v(1278, 150) * mm, "mid": v(1282, 154) * mm, "end": v(1286, 150) * mm});
            skLineSegment(sketch, "E17.7.69.0", {"start": v(1278, 150) * mm, "end": v(1278, 100) * mm});
            skArc(sketch, "E17.10.69.0", {"start": v(1286, 100) * mm, "mid": v(1282, 96) * mm, "end": v(1278, 100) * mm});
            skLineSegment(sketch, "E17.0.70.0", {"start": v(1304, 150) * mm, "end": v(1304, 100) * mm});
            skArc(sketch, "E17.3.70.0", {"start": v(1296, 150) * mm, "mid": v(1300, 154) * mm, "end": v(1304, 150) * mm});
            skLineSegment(sketch, "E17.7.70.0", {"start": v(1296, 150) * mm, "end": v(1296, 100) * mm});
            skArc(sketch, "E17.10.70.0", {"start": v(1304, 100) * mm, "mid": v(1300, 96) * mm, "end": v(1296, 100) * mm});
            skLineSegment(sketch, "E17.0.71.0", {"start": v(1322, 150) * mm, "end": v(1322, 100) * mm});
            skArc(sketch, "E17.3.71.0", {"start": v(1314, 150) * mm, "mid": v(1318, 154) * mm, "end": v(1322, 150) * mm});
            skLineSegment(sketch, "E17.7.71.0", {"start": v(1314, 150) * mm, "end": v(1314, 100) * mm});
            skArc(sketch, "E17.10.71.0", {"start": v(1322, 100) * mm, "mid": v(1318, 96) * mm, "end": v(1314, 100) * mm});
            skLineSegment(sketch, "E17.0.72.0", {"start": v(1340, 150) * mm, "end": v(1340, 100) * mm});
            skArc(sketch, "E17.3.72.0", {"start": v(1332, 150) * mm, "mid": v(1336, 154) * mm, "end": v(1340, 150) * mm});
            skLineSegment(sketch, "E17.7.72.0", {"start": v(1332, 150) * mm, "end": v(1332, 100) * mm});
            skArc(sketch, "E17.10.72.0", {"start": v(1340, 100) * mm, "mid": v(1336, 96) * mm, "end": v(1332, 100) * mm});
            skLineSegment(sketch, "E17.0.73.0", {"start": v(1358, 150) * mm, "end": v(1358, 100) * mm});
            skArc(sketch, "E17.3.73.0", {"start": v(1350, 150) * mm, "mid": v(1354, 154) * mm, "end": v(1358, 150) * mm});
            skLineSegment(sketch, "E17.7.73.0", {"start": v(1350, 150) * mm, "end": v(1350, 100) * mm});
            skArc(sketch, "E17.10.73.0", {"start": v(1358, 100) * mm, "mid": v(1354, 96) * mm, "end": v(1350, 100) * mm});
            skLineSegment(sketch, "E17.0.74.0", {"start": v(1376, 150) * mm, "end": v(1376, 100) * mm});
            skArc(sketch, "E17.3.74.0", {"start": v(1368, 150) * mm, "mid": v(1372, 154) * mm, "end": v(1376, 150) * mm});
            skLineSegment(sketch, "E17.7.74.0", {"start": v(1368, 150) * mm, "end": v(1368, 100) * mm});
            skArc(sketch, "E17.10.74.0", {"start": v(1376, 100) * mm, "mid": v(1372, 96) * mm, "end": v(1368, 100) * mm});
            skLineSegment(sketch, "E17.0.75.0", {"start": v(1394, 150) * mm, "end": v(1394, 100) * mm});
            skArc(sketch, "E17.3.75.0", {"start": v(1386, 150) * mm, "mid": v(1390, 154) * mm, "end": v(1394, 150) * mm});
            skLineSegment(sketch, "E17.7.75.0", {"start": v(1386, 150) * mm, "end": v(1386, 100) * mm});
            skArc(sketch, "E17.10.75.0", {"start": v(1394, 100) * mm, "mid": v(1390, 96) * mm, "end": v(1386, 100) * mm});
            skLineSegment(sketch, "E17.0.76.0", {"start": v(1412, 150) * mm, "end": v(1412, 100) * mm});
            skArc(sketch, "E17.3.76.0", {"start": v(1404, 150) * mm, "mid": v(1408, 154) * mm, "end": v(1412, 150) * mm});
            skLineSegment(sketch, "E17.7.76.0", {"start": v(1404, 150) * mm, "end": v(1404, 100) * mm});
            skArc(sketch, "E17.10.76.0", {"start": v(1412, 100) * mm, "mid": v(1408, 96) * mm, "end": v(1404, 100) * mm});
            skLineSegment(sketch, "E17.0.77.0", {"start": v(1430, 150) * mm, "end": v(1430, 100) * mm});
            skArc(sketch, "E17.3.77.0", {"start": v(1422, 150) * mm, "mid": v(1426, 154) * mm, "end": v(1430, 150) * mm});
            skLineSegment(sketch, "E17.7.77.0", {"start": v(1422, 150) * mm, "end": v(1422, 100) * mm});
            skArc(sketch, "E17.10.77.0", {"start": v(1430, 100) * mm, "mid": v(1426, 96) * mm, "end": v(1422, 100) * mm});
            skLineSegment(sketch, "E17.0.78.0", {"start": v(1448, 150) * mm, "end": v(1448, 100) * mm});
            skArc(sketch, "E17.3.78.0", {"start": v(1440, 150) * mm, "mid": v(1444, 154) * mm, "end": v(1448, 150) * mm});
            skLineSegment(sketch, "E17.7.78.0", {"start": v(1440, 150) * mm, "end": v(1440, 100) * mm});
            skArc(sketch, "E17.10.78.0", {"start": v(1448, 100) * mm, "mid": v(1444, 96) * mm, "end": v(1440, 100) * mm});
            skLineSegment(sketch, "E17.0.79.0", {"start": v(1466, 150) * mm, "end": v(1466, 100) * mm});
            skArc(sketch, "E17.3.79.0", {"start": v(1458, 150) * mm, "mid": v(1462, 154) * mm, "end": v(1466, 150) * mm});
            skLineSegment(sketch, "E17.7.79.0", {"start": v(1458, 150) * mm, "end": v(1458, 100) * mm});
            skArc(sketch, "E17.10.79.0", {"start": v(1466, 100) * mm, "mid": v(1462, 96) * mm, "end": v(1458, 100) * mm});
            skLineSegment(sketch, "E17.0.80.0", {"start": v(1484, 150) * mm, "end": v(1484, 100) * mm});
            skArc(sketch, "E17.3.80.0", {"start": v(1476, 150) * mm, "mid": v(1480, 154) * mm, "end": v(1484, 150) * mm});
            skLineSegment(sketch, "E17.7.80.0", {"start": v(1476, 150) * mm, "end": v(1476, 100) * mm});
            skArc(sketch, "E17.10.80.0", {"start": v(1484, 100) * mm, "mid": v(1480, 96) * mm, "end": v(1476, 100) * mm});
            skLineSegment(sketch, "E17.0.81.0", {"start": v(1502, 150) * mm, "end": v(1502, 100) * mm});
            skArc(sketch, "E17.3.81.0", {"start": v(1494, 150) * mm, "mid": v(1498, 154) * mm, "end": v(1502, 150) * mm});
            skLineSegment(sketch, "E17.7.81.0", {"start": v(1494, 150) * mm, "end": v(1494, 100) * mm});
            skArc(sketch, "E17.10.81.0", {"start": v(1502, 100) * mm, "mid": v(1498, 96) * mm, "end": v(1494, 100) * mm});
            skLineSegment(sketch, "E17.0.82.0", {"start": v(1520, 150) * mm, "end": v(1520, 100) * mm});
            skArc(sketch, "E17.3.82.0", {"start": v(1512, 150) * mm, "mid": v(1516, 154) * mm, "end": v(1520, 150) * mm});
            skLineSegment(sketch, "E17.7.82.0", {"start": v(1512, 150) * mm, "end": v(1512, 100) * mm});
            skArc(sketch, "E17.10.82.0", {"start": v(1520, 100) * mm, "mid": v(1516, 96) * mm, "end": v(1512, 100) * mm});
            skLineSegment(sketch, "E17.0.83.0", {"start": v(1538, 150) * mm, "end": v(1538, 100) * mm});
            skArc(sketch, "E17.3.83.0", {"start": v(1530, 150) * mm, "mid": v(1534, 154) * mm, "end": v(1538, 150) * mm});
            skLineSegment(sketch, "E17.7.83.0", {"start": v(1530, 150) * mm, "end": v(1530, 100) * mm});
            skArc(sketch, "E17.10.83.0", {"start": v(1538, 100) * mm, "mid": v(1534, 96) * mm, "end": v(1530, 100) * mm});
            skSolve(sketch);
        }
        {
            var Q0;
            Q0 = qSketchRegion(id + "F4", true);
            extrude(context, id + "F5", {"entities" : qUnion([Q0]), "operationType" : NewBodyOperationType.REMOVE, "endBound" : BoundingType.UP_TO_NEXT, "oppositeDirection" : true, "depth" : 25 * mm, "offsetDistance" : 25 * mm});
        }
        {
            var Q0;
            Q0=makeQuery(id+"F1.opExtrude","SWEPT_FACE",FACE,{"disambiguationData":[OSD([sQuery(id+"F0.wireOp",EDGE,"E0")])]});
            var sketch = newSketch(context, id + "F6", { "sketchPlane" : qUnion([Q0])});
            skLineSegment(sketch, "E18.bottom", {"start": v(1570, -900) * mm, "end": v(20, -900) * mm});
            skLineSegment(sketch, "E18.top", {"start": v(1570, -60) * mm, "end": v(20, -60) * mm});
            skLineSegment(sketch, "E18.left", {"start": v(1570, -900) * mm, "end": v(1570, -60) * mm});
            skLineSegment(sketch, "E18.right", {"start": v(20, -900) * mm, "end": v(20, -60) * mm});
            skSolve(sketch);
        }
        {
            var Q0;
            Q0 = qSketchRegion(id + "F6", true);
            extrude(context, id + "F7", {"entities" : qUnion([Q0]), "operationType" : NewBodyOperationType.ADD, "depth" : 74 * mm, "offsetDistance" : 25 * mm});
        }
        {
            var Q0;
            Q0=makeQuery(id+"F7.opExtrude","CAP_FACE",FACE,{"disambiguationData":[OSD([sQuery(id+"F6.wireOp",EDGE,"E18.bottom"),sQuery(id+"F6.wireOp",EDGE,"E18.top"),sQuery(id+"F6.wireOp",EDGE,"E18.left"),sQuery(id+"F6.wireOp",EDGE,"E18.right")])],"isStart":false});
            var sketch = newSketch(context, id + "F8", { "sketchPlane" : qUnion([Q0])});
            skLineSegment(sketch, "E19.bottom", {"start": v(20, -60) * mm, "end": v(1570, -60) * mm});
            skLineSegment(sketch, "E19.top", {"start": v(20, -810) * mm, "end": v(1570, -810) * mm});
            skLineSegment(sketch, "E19.left", {"start": v(20, -60) * mm, "end": v(20, -810) * mm});
            skLineSegment(sketch, "E19.right", {"start": v(1570, -60) * mm, "end": v(1570, -810) * mm});
            skSolve(sketch);
        }
        {
            var Q0;
            Q0 = qSketchRegion(id + "F8", true);
            extrude(context, id + "F9", {"entities" : qUnion([Q0]), "operationType" : NewBodyOperationType.ADD, "depth" : 240 * mm, "offsetDistance" : 25 * mm});
        }
        {
            var Q0;
            Q0=makeQuery(id+"F1.opExtrude","SWEPT_FACE",FACE,{"disambiguationData":[OSD([sQuery(id+"F0.wireOp",EDGE,"E4")])]});
            var sketch = newSketch(context, id + "F10", { "sketchPlane" : qUnion([Q0])});
            skCircle(sketch, "E20", {"center": v(780, 829) * mm, "radius": 20 * mm});
            skSolve(sketch);
        }
        {
            var Q0;
            Q0 = qSketchRegion(id + "F10", true);
            extrude(context, id + "F11", {"entities" : qUnion([Q0]), "operationType" : NewBodyOperationType.ADD, "depth" : 5 * mm, "offsetDistance" : 25 * mm, "hasDraft" : true, "draftAngle" : 45 * degree, "draftPullDirection" : true});
        }
        {
            var Q0;
            Q0=makeQuery(id+"F11.opExtrude","CAP_FACE",FACE,{"disambiguationData":[OSD([sQuery(id+"F10.wireOp",EDGE,"E20")])],"isStart":false});
            var sketch = newSketch(context, id + "F12", { "sketchPlane" : qUnion([Q0])});
            skCircle(sketch, "E21", {"center": v(780, 829) * mm, "radius": 12.5 * mm});
            skSolve(sketch);
        }
        {
            var Q0;
            Q0 = qSketchRegion(id + "F12", true);
            extrude(context, id + "F13", {"entities" : qUnion([Q0]), "operationType" : NewBodyOperationType.ADD, "depth" : 200 * mm, "offsetDistance" : 25 * mm});
        }
        {
            var Q0;
            Q0=makeQuery(id+"F13.opExtrude","CAP_FACE",FACE,{"disambiguationData":[OSD([sQuery(id+"F12.wireOp",EDGE,"E21")])],"isStart":false});
            var sketch = newSketch(context, id + "F14", { "sketchPlane" : qUnion([Q0])});
            skCircle(sketch, "E22", {"center": v(780, 829) * mm, "radius": 11.5 * mm});
            skSolve(sketch);
        }
        {
            var Q0;
            Q0 = qSketchRegion(id + "F14", true);
            extrude(context, id + "F15", {"entities" : qUnion([Q0]), "operationType" : NewBodyOperationType.ADD, "depth" : 1 * mm, "offsetDistance" : 25 * mm});
        }
        {
            var Q0;
            Q0=makeQuery(id+"F15.opExtrude","CAP_FACE",FACE,{"disambiguationData":[OSD([sQuery(id+"F14.wireOp",EDGE,"E22")])],"isStart":false});
            var sketch = newSketch(context, id + "F16", { "sketchPlane" : qUnion([Q0])});
            skCircle(sketch, "E23", {"center": v(780, 829) * mm, "radius": 13 * mm});
            skSolve(sketch);
        }
        {
            var Q0;
            Q0 = qSketchRegion(id + "F16", true);
            extrude(context, id + "F17", {"entities" : qUnion([Q0]), "operationType" : NewBodyOperationType.ADD, "depth" : 50 * mm, "offsetDistance" : 25 * mm});
        }
        {
            var Q0;
            Q0=makeQuery(id+"F17.opExtrude","CAP_FACE",FACE,{"disambiguationData":[OSD([sQuery(id+"F16.wireOp",EDGE,"E23")])],"isStart":false});
            var sketch = newSketch(context, id + "F18", { "sketchPlane" : qUnion([Q0])});
            skPoint(sketch, "E24", {"position": v(780, 829) * mm});
            skSolve(sketch);
        }
        {
            var Q0;
            Q0=qCreatedBy(makeId("Right.planeOp"),FACE);
            var Q1;
            Q1=sQuery(id+"F18.wireOp",VERTEX,"E24");
            cPlane(context, id + "F19", {"entities" : qUnion([Q0, Q1]), "cplaneType" : CPlaneType.PLANE_POINT, "offset" : 25 * mm, "width" : 150 * mm, "height" : 150 * mm});
        }
        {
            var Q0;
            Q0=qCreatedBy(id+"F19.planeOp",FACE);
            var sketch = newSketch(context, id + "F20", { "sketchPlane" : qUnion([Q0])});
            skLineSegment(sketch, "E25", {"start": v(816, 296) * mm, "end": v(801.86, 310.14) * mm});
            skLineSegment(sketch, "E26", {"start": v(816, 296) * mm, "end": v(816, 315.86) * mm, "construction": true});
            skSolve(sketch);
        }
        {
            var Q0;
            Q0=sQuery(id+"F20.wireOp",VERTEX,"E25.end");
            var Q1;
            Q1=sQuery(id+"F20.wireOp",EDGE,"E25");
            cPlane(context, id + "F21", {"entities" : qUnion([Q0, Q1]), "cplaneType" : CPlaneType.LINE_POINT, "offset" : 25 * mm, "width" : 150 * mm, "height" : 150 * mm});
        }
        {
            var Q0;
            Q0=qCreatedBy(id+"F21.planeOp",FACE);
            var sketch = newSketch(context, id + "F22", { "sketchPlane" : qUnion([Q0])});
            skCircle(sketch, "E27", {"center": v(780, 786.3) * mm, "radius": 12.5 * mm});
            skSolve(sketch);
        }
        {
            var Q0;
            Q0 = qSketchRegion(id + "F22", true);
            extrude(context, id + "F23", {"entities" : qUnion([Q0]), "operationType" : NewBodyOperationType.ADD, "endBound" : BoundingType.UP_TO_NEXT, "oppositeDirection" : true, "depth" : 25 * mm, "offsetDistance" : 25 * mm});
        }
        {
            var Q0;
            Q0=makeQuery(id+"F23.opExtrude","CAP_FACE",FACE,{"disambiguationData":[OSD([sQuery(id+"F22.wireOp",EDGE,"E27")])],"isStart":true});
            var sketch = newSketch(context, id + "F24", { "sketchPlane" : qUnion([Q0])});
            skCircle(sketch, "E28", {"center": v(780, 786.3) * mm, "radius": 11.5 * mm});
            skSolve(sketch);
        }
        {
            var Q0;
            Q0 = qSketchRegion(id + "F24", true);
            extrude(context, id + "F25", {"entities" : qUnion([Q0]), "operationType" : NewBodyOperationType.ADD, "depth" : 1 * mm, "offsetDistance" : 25 * mm});
        }
        {
            var Q0;
            Q0=makeQuery(id+"F25.opExtrude","CAP_FACE",FACE,{"disambiguationData":[OSD([sQuery(id+"F24.wireOp",EDGE,"E28")])],"isStart":false});
            var sketch = newSketch(context, id + "F26", { "sketchPlane" : qUnion([Q0])});
            skCircle(sketch, "E29", {"center": v(780, 786.3) * mm, "radius": 14 * mm});
            skSolve(sketch);
        }
        {
            var Q0;
            Q0 = qSketchRegion(id + "F26", true);
            extrude(context, id + "F27", {"entities" : qUnion([Q0]), "operationType" : NewBodyOperationType.ADD, "depth" : 30 * mm, "offsetDistance" : 25 * mm, "hasDraft" : true, "draftAngle" : 5 * degree});
        }
        {
            var Q0;
            Q0=makeQuery(id+"F27.opExtrude","CAP_FACE",FACE,{"disambiguationData":[OSD([sQuery(id+"F26.wireOp",EDGE,"E29")])],"isStart":false});
            var sketch = newSketch(context, id + "F28", { "sketchPlane" : qUnion([Q0])});
            skCircle(sketch, "E30", {"center": v(780, 786.3) * mm, "radius": 12.62 * mm});
            skSolve(sketch);
        }
        {
            var Q0;
            Q0 = qSketchRegion(id + "F28", true);
            extrude(context, id + "F29", {"entities" : qUnion([Q0]), "operationType" : NewBodyOperationType.REMOVE, "oppositeDirection" : true, "depth" : 2 * mm, "offsetDistance" : 25 * mm});
        }
        {
            var Q0;
            Q0=makeQuery(id+"F29.boolean.opBoolean","COPY",FACE,{"derivedFrom":makeQuery(id+"F29.opExtrude","CAP_FACE",FACE,{"disambiguationData":[OSD([sQuery(id+"F28.wireOp",EDGE,"E30")])],"isStart":false})});
            var sketch = newSketch(context, id + "F30", { "sketchPlane" : qUnion([Q0])});
            skCircle(sketch, "E31", {"center": v(780, 786.3) * mm, "radius": 11.62 * mm});
            skSolve(sketch);
        }
        {
            var Q0;
            Q0 = qSketchRegion(id + "F30", true);
            extrude(context, id + "F31", {"entities" : qUnion([Q0]), "operationType" : NewBodyOperationType.ADD, "depth" : 4 * mm, "offsetDistance" : 25 * mm, "hasDraft" : true, "draftAngle" : 45 * degree, "draftPullDirection" : true});
        }
        {
            var Q0;
            Q0=makeQuery(id+"F31.opExtrude","CAP_EDGE",EDGE,{"disambiguationData":[OSD([sQuery(id+"F30.wireOp",EDGE,"E31")])],"isStart":false});
            fillet(context, id + "F32", {"entities" : qUnion([Q0]), "radius" : 13.5 * mm, "tangentPropagation" : true, "allowEdgeOverflow" : false});
        }
        {
            var Q0;
            Q0=makeQuery(id+"F18.imprint","IMPRINT",FACE,{"disambiguationData":[TD([[makeQuery(id+"F18.imprint","IMPRINT",EDGE,{"derivedFrom":makeQuery(id+"F17.opExtrude","CAP_EDGE",EDGE,{"disambiguationData":[OSD([sQuery(id+"F16.wireOp",EDGE,"E23")])],"isStart":false})}),1.0]])]});
            var sketch = newSketch(context, id + "F33", { "sketchPlane" : qUnion([Q0])});
            skCircle(sketch, "E32", {"center": v(780, 829) * mm, "radius": 10 * mm});
            skSolve(sketch);
        }
        {
            var Q0;
            Q0=qCreatedBy(id+"F19.planeOp",FACE);
            var sketch = newSketch(context, id + "F34", { "sketchPlane" : qUnion([Q0])});
            skLineSegment(sketch, "E33", {"start": v(829, 321) * mm, "end": v(829, 350) * mm});
            skLineSegment(sketch, "E34", {"start": v(809.26, 378.18) * mm, "end": v(661.2, 432.08) * mm});
            skLineSegment(sketch, "E35", {"start": v(641.06, 417.98) * mm, "end": v(641.06, 399.4) * mm});
            skPoint(sketch, "E36.visualSharp", {"position": v(829, 371) * mm});
            skArc(sketch, "E36.filletArc", {"start": v(829, 350) * mm, "mid": v(823.57, 367.2) * mm, "end": v(809.26, 378.18) * mm});
            skPoint(sketch, "E37.visualSharp", {"position": v(641.06, 439.4) * mm});
            skArc(sketch, "E37.filletArc", {"start": v(661.2, 432.08) * mm, "mid": v(647.46, 430.27) * mm, "end": v(641.06, 417.98) * mm});
            skSolve(sketch);
        }
        {
            var Q0;
            Q0=makeQuery(id+"F33.imprint","IMPRINT",FACE,{"disambiguationData":[TD([[makeQuery(id+"F33.imprint","IMPRINT",EDGE,{"derivedFrom":sQuery(id+"F33.wireOp",EDGE,"E32")}),1.0]])]});
            var Q1;
            Q1=sQuery(id+"F34.wireOp",EDGE,"E33");
            var Q2;
            Q2=sQuery(id+"F34.wireOp",EDGE,"E36.filletArc");
            var Q3;
            Q3=sQuery(id+"F34.wireOp",EDGE,"E34");
            var Q4;
            Q4=sQuery(id+"F34.wireOp",EDGE,"E37.filletArc");
            var Q5;
            Q5=sQuery(id+"F34.wireOp",EDGE,"E35");
            sweep(context, id + "F35", {"operationType" : NewBodyOperationType.ADD, "profiles" : qUnion([Q0]), "path" : qUnion([Q1, Q2, Q3, Q4, Q5])});
        }
        {
            var Q0;
            Q0=makeQuery(id+"F35.opSweep","CAP_FACE",FACE,{"disambiguationData":[OSD([sQuery(id+"F33.wireOp",EDGE,"E32"),sQuery(id+"F34.wireOp",VERTEX,"E35.end")])],"isStart":false});
            var sketch = newSketch(context, id + "F36", { "sketchPlane" : qUnion([Q0])});
            skCircle(sketch, "E38", {"center": v(780, -641.06) * mm, "radius": 10.5 * mm});
            skSolve(sketch);
        }
        {
            var Q0;
            Q0 = qSketchRegion(id + "F36", true);
            extrude(context, id + "F37", {"entities" : qUnion([Q0]), "operationType" : NewBodyOperationType.ADD, "depth" : 10 * mm, "offsetDistance" : 25 * mm});
        }
        {
            var Q0;
            Q0=makeQuery(id+"F37.opExtrude","CAP_EDGE",EDGE,{"disambiguationData":[OSD([sQuery(id+"F36.wireOp",EDGE,"E38")])],"isStart":true});
            var Q1;
            Q1=makeQuery(id+"F37.opExtrude","CAP_EDGE",EDGE,{"disambiguationData":[OSD([sQuery(id+"F36.wireOp",EDGE,"E38")])],"isStart":false});
            fillet(context, id + "F38", {"entities" : qUnion([Q0, Q1]), "radius" : 2.5 * mm, "tangentPropagation" : true, "allowEdgeOverflow" : false});
        }
        {
            var Q0;
            Q0=makeQuery(id+"F37.opExtrude","CAP_FACE",FACE,{"disambiguationData":[OSD([sQuery(id+"F36.wireOp",EDGE,"E38")])],"isStart":false});
            var sketch = newSketch(context, id + "F39", { "sketchPlane" : qUnion([Q0])});
            skCircle(sketch, "E39", {"center": v(780, -641.06) * mm, "radius": 8 * mm});
            skSolve(sketch);
        }
        {
            var Q0;
            Q0 = qSketchRegion(id + "F39", true);
            extrude(context, id + "F40", {"entities" : qUnion([Q0]), "operationType" : NewBodyOperationType.ADD, "depth" : 1.5 * mm, "offsetDistance" : 25 * mm});
        }
        {
            var Q0;
            Q0=makeQuery(id+"F9.opExtrude","CAP_FACE",FACE,{"disambiguationData":[OSD([sQuery(id+"F8.wireOp",EDGE,"E19.bottom"),sQuery(id+"F8.wireOp",EDGE,"E19.top"),sQuery(id+"F8.wireOp",EDGE,"E19.left"),sQuery(id+"F8.wireOp",EDGE,"E19.right")])],"isStart":false});
            var sketch = newSketch(context, id + "F41", { "sketchPlane" : qUnion([Q0])});
            skLineSegment(sketch, "E40.bottom", {"start": v(20, -60) * mm, "end": v(50, -60) * mm});
            skLineSegment(sketch, "E40.top", {"start": v(20, -90) * mm, "end": v(50, -90) * mm});
            skLineSegment(sketch, "E40.left", {"start": v(20, -60) * mm, "end": v(20, -90) * mm});
            skLineSegment(sketch, "E40.right", {"start": v(50, -60) * mm, "end": v(50, -90) * mm});
            skLineSegment(sketch, "E41.bottom", {"start": v(1570, -60) * mm, "end": v(1540, -60) * mm});
            skLineSegment(sketch, "E41.top", {"start": v(1570, -90) * mm, "end": v(1540, -90) * mm});
            skLineSegment(sketch, "E41.left", {"start": v(1570, -60) * mm, "end": v(1570, -90) * mm});
            skLineSegment(sketch, "E41.right", {"start": v(1540, -60) * mm, "end": v(1540, -90) * mm});
            skLineSegment(sketch, "E42.bottom", {"start": v(20, -810) * mm, "end": v(50, -810) * mm});
            skLineSegment(sketch, "E42.top", {"start": v(20, -780) * mm, "end": v(50, -780) * mm});
            skLineSegment(sketch, "E42.left", {"start": v(20, -810) * mm, "end": v(20, -780) * mm});
            skLineSegment(sketch, "E42.right", {"start": v(50, -810) * mm, "end": v(50, -780) * mm});
            skLineSegment(sketch, "E43.bottom", {"start": v(1570, -810) * mm, "end": v(1540, -810) * mm});
            skLineSegment(sketch, "E43.top", {"start": v(1570, -780) * mm, "end": v(1540, -780) * mm});
            skLineSegment(sketch, "E43.left", {"start": v(1570, -810) * mm, "end": v(1570, -780) * mm});
            skLineSegment(sketch, "E43.right", {"start": v(1540, -810) * mm, "end": v(1540, -780) * mm});
            skLineSegment(sketch, "E44.bottom", {"start": v(780, -60) * mm, "end": v(810, -60) * mm});
            skLineSegment(sketch, "E44.top", {"start": v(780, -90) * mm, "end": v(810, -90) * mm});
            skLineSegment(sketch, "E44.left", {"start": v(780, -60) * mm, "end": v(780, -90) * mm});
            skLineSegment(sketch, "E44.right", {"start": v(810, -60) * mm, "end": v(810, -90) * mm});
            skLineSegment(sketch, "E45.bottom", {"start": v(780, -810) * mm, "end": v(810, -810) * mm});
            skLineSegment(sketch, "E45.top", {"start": v(780, -780) * mm, "end": v(810, -780) * mm});
            skLineSegment(sketch, "E45.left", {"start": v(780, -810) * mm, "end": v(780, -780) * mm});
            skLineSegment(sketch, "E45.right", {"start": v(810, -810) * mm, "end": v(810, -780) * mm});
            skSolve(sketch);
        }
        {
            var Q0;
            Q0 = qSketchRegion(id + "F41", true);
            extrude(context, id + "F42", {"entities" : qUnion([Q0]), "operationType" : NewBodyOperationType.ADD, "depth" : 531 * mm, "offsetDistance" : 25 * mm});
        }
        {
            var Q0;
            Q0=makeQuery(id+"F42.boolean.opBoolean","MERGE",FACE,{"derivedFrom":[makeQuery(id+"F9.boolean.opBoolean","MERGE",FACE,{"derivedFrom":[makeQuery(id+"F7.opExtrude","SWEPT_FACE",FACE,{"disambiguationData":[OSD([sQuery(id+"F6.wireOp",EDGE,"E18.left")])]}),makeQuery(id+"F9.opExtrude","SWEPT_FACE",FACE,{"disambiguationData":[OSD([sQuery(id+"F8.wireOp",EDGE,"E19.right")])]})]}),makeQuery(id+"F42.opExtrude","SWEPT_FACE",FACE,{"disambiguationData":[OSD([sQuery(id+"F41.wireOp",EDGE,"E41.left")])]}),makeQuery(id+"F42.opExtrude","SWEPT_FACE",FACE,{"disambiguationData":[OSD([sQuery(id+"F41.wireOp",EDGE,"E43.left")])]})]});
            var sketch = newSketch(context, id + "F43", { "sketchPlane" : qUnion([Q0])});
            skLineSegment(sketch, "E46.bottom", {"start": v(60, -725) * mm, "end": v(810, -725) * mm});
            skLineSegment(sketch, "E46.top", {"start": v(60, -695) * mm, "end": v(810, -695) * mm});
            skLineSegment(sketch, "E46.left", {"start": v(60, -725) * mm, "end": v(60, -695) * mm});
            skLineSegment(sketch, "E46.right", {"start": v(810, -725) * mm, "end": v(810, -695) * mm});
            skSolve(sketch);
        }
        {
            var Q0;
            Q0 = qSketchRegion(id + "F43", true);
            var Q1;
            Q1=makeQuery(id+"F42.boolean.opBoolean","MERGE",FACE,{"derivedFrom":[makeQuery(id+"F9.boolean.opBoolean","MERGE",FACE,{"derivedFrom":[makeQuery(id+"F7.opExtrude","SWEPT_FACE",FACE,{"disambiguationData":[OSD([sQuery(id+"F6.wireOp",EDGE,"E18.right")])]}),makeQuery(id+"F9.opExtrude","SWEPT_FACE",FACE,{"disambiguationData":[OSD([sQuery(id+"F8.wireOp",EDGE,"E19.left")])]})]}),makeQuery(id+"F42.opExtrude","SWEPT_FACE",FACE,{"disambiguationData":[OSD([sQuery(id+"F41.wireOp",EDGE,"E40.left")])]}),makeQuery(id+"F42.opExtrude","SWEPT_FACE",FACE,{"disambiguationData":[OSD([sQuery(id+"F41.wireOp",EDGE,"E42.left")])]})]});
            extrude(context, id + "F44", {"entities" : qUnion([Q0]), "operationType" : NewBodyOperationType.ADD, "endBound" : BoundingType.UP_TO_SURFACE, "oppositeDirection" : true, "depth" : 25 * mm, "endBoundEntityFace" : qUnion([Q1]), "offsetDistance" : 25 * mm});
        }
        {
            var Q0;
            Q0=makeQuery(id+"F3.boolean.opBoolean","COPY",FACE,{"derivedFrom":makeQuery(id+"F3.opExtrude","CAP_FACE",FACE,{"disambiguationData":[OSD([sQuery(id+"F2.wireOp",EDGE,"enBUSuRZ-7T91-VFCD-VRLf-bCCln2bcZ8a5.bottom"),sQuery(id+"F2.wireOp",EDGE,"enBUSuRZ-7T91-VFCD-VRLf-bCCln2bcZ8a5.top"),sQuery(id+"F2.wireOp",EDGE,"enBUSuRZ-7T91-VFCD-VRLf-bCCln2bcZ8a5.left"),sQuery(id+"F2.wireOp",EDGE,"enBUSuRZ-7T91-VFCD-VRLf-bCCln2bcZ8a5.right")])],"isStart":false})});
            var Q1;
            Q1=makeQuery(id+"F3.boolean.opBoolean","COPY",FACE,{"derivedFrom":makeQuery(id+"F3.opExtrude","CAP_FACE",FACE,{"disambiguationData":[OSD([sQuery(id+"F2.wireOp",EDGE,"lAeq3iL0-EvoZ-US1E-NuhF-w5OJPEajD2Mo.bottom"),sQuery(id+"F2.wireOp",EDGE,"lAeq3iL0-EvoZ-US1E-NuhF-w5OJPEajD2Mo.top"),sQuery(id+"F2.wireOp",EDGE,"lAeq3iL0-EvoZ-US1E-NuhF-w5OJPEajD2Mo.left"),sQuery(id+"F2.wireOp",EDGE,"lAeq3iL0-EvoZ-US1E-NuhF-w5OJPEajD2Mo.right")])],"isStart":false})});
            var Q2;
            Q2=makeQuery(id+"F3.boolean.opBoolean","COPY",FACE,{"derivedFrom":makeQuery(id+"F3.opExtrude","CAP_FACE",FACE,{"disambiguationData":[OSD([sQuery(id+"F2.wireOp",EDGE,"Z7KGXwbD-Vz0g-bElp-JuvT-9JmmRMYruGMK.bottom"),sQuery(id+"F2.wireOp",EDGE,"Z7KGXwbD-Vz0g-bElp-JuvT-9JmmRMYruGMK.top"),sQuery(id+"F2.wireOp",EDGE,"Z7KGXwbD-Vz0g-bElp-JuvT-9JmmRMYruGMK.left"),sQuery(id+"F2.wireOp",EDGE,"Z7KGXwbD-Vz0g-bElp-JuvT-9JmmRMYruGMK.right")])],"isStart":false})});
            var Q3;
            Q3=makeQuery(id+"F3.boolean.opBoolean","COPY",FACE,{"derivedFrom":makeQuery(id+"F3.opExtrude","CAP_FACE",FACE,{"disambiguationData":[OSD([sQuery(id+"F2.wireOp",EDGE,"74659be0-351a-4009-a0a2-7d629be29af25.MirrorCS"),sQuery(id+"F2.wireOp",EDGE,"74659be0-351a-4009-a0a2-7d629be29af28.MirrorCS"),sQuery(id+"F2.wireOp",EDGE,"74659be0-351a-4009-a0a2-7d629be29af29.MirrorCS"),sQuery(id+"F2.wireOp",EDGE,"74659be0-351a-4009-a0a2-7d629be29af211.MirrorCS")])],"isStart":false})});
            var Q4;
            Q4=makeQuery(id+"F3.boolean.opBoolean","COPY",FACE,{"derivedFrom":makeQuery(id+"F3.opExtrude","CAP_FACE",FACE,{"disambiguationData":[OSD([sQuery(id+"F2.wireOp",EDGE,"74659be0-351a-4009-a0a2-7d629be29af20.MirrorCS"),sQuery(id+"F2.wireOp",EDGE,"74659be0-351a-4009-a0a2-7d629be29af21.MirrorCS"),sQuery(id+"F2.wireOp",EDGE,"74659be0-351a-4009-a0a2-7d629be29af22.MirrorCS"),sQuery(id+"F2.wireOp",EDGE,"74659be0-351a-4009-a0a2-7d629be29af24.MirrorCS")])],"isStart":false})});
            var Q5;
            Q5=makeQuery(id+"F3.boolean.opBoolean","COPY",FACE,{"derivedFrom":makeQuery(id+"F3.opExtrude","CAP_FACE",FACE,{"disambiguationData":[OSD([sQuery(id+"F2.wireOp",EDGE,"74659be0-351a-4009-a0a2-7d629be29af23.MirrorCS"),sQuery(id+"F2.wireOp",EDGE,"74659be0-351a-4009-a0a2-7d629be29af26.MirrorCS"),sQuery(id+"F2.wireOp",EDGE,"74659be0-351a-4009-a0a2-7d629be29af27.MirrorCS"),sQuery(id+"F2.wireOp",EDGE,"74659be0-351a-4009-a0a2-7d629be29af210.MirrorCS")])],"isStart":false})});
            var Q6;
            Q6=makeQuery(id+"F3.boolean.opBoolean","COPY",FACE,{"derivedFrom":makeQuery(id+"F3.opExtrude","CAP_FACE",FACE,{"disambiguationData":[OSD([sQuery(id+"F2.wireOp",EDGE,"eHqmKlBl-sdoI-ErtD-Op6X-hP3XPX0j9z9X.bottom"),sQuery(id+"F2.wireOp",EDGE,"eHqmKlBl-sdoI-ErtD-Op6X-hP3XPX0j9z9X.top"),sQuery(id+"F2.wireOp",EDGE,"eHqmKlBl-sdoI-ErtD-Op6X-hP3XPX0j9z9X.left"),sQuery(id+"F2.wireOp",EDGE,"eHqmKlBl-sdoI-ErtD-Op6X-hP3XPX0j9z9X.right")])],"isStart":false})});
            var Q7;
            Q7=makeQuery(id+"F3.boolean.opBoolean","COPY",FACE,{"derivedFrom":makeQuery(id+"F3.opExtrude","CAP_FACE",FACE,{"disambiguationData":[OSD([sQuery(id+"F2.wireOp",EDGE,"FPaW8bXa-9Qry-Kjjf-KrIU-xUhFQ1uwAMGn.bottom"),sQuery(id+"F2.wireOp",EDGE,"FPaW8bXa-9Qry-Kjjf-KrIU-xUhFQ1uwAMGn.top"),sQuery(id+"F2.wireOp",EDGE,"FPaW8bXa-9Qry-Kjjf-KrIU-xUhFQ1uwAMGn.left"),sQuery(id+"F2.wireOp",EDGE,"FPaW8bXa-9Qry-Kjjf-KrIU-xUhFQ1uwAMGn.right")])],"isStart":false})});
            var Q8;
            Q8=makeQuery(id+"F3.boolean.opBoolean","COPY",FACE,{"derivedFrom":makeQuery(id+"F3.opExtrude","CAP_FACE",FACE,{"disambiguationData":[OSD([sQuery(id+"F2.wireOp",EDGE,"E12.bottom"),sQuery(id+"F2.wireOp",EDGE,"E12.top"),sQuery(id+"F2.wireOp",EDGE,"E12.left"),sQuery(id+"F2.wireOp",EDGE,"E12.right")])],"isStart":false})});
            var Q9;
            Q9=makeQuery(id+"F3.boolean.opBoolean","COPY",FACE,{"derivedFrom":makeQuery(id+"F3.opExtrude","CAP_FACE",FACE,{"disambiguationData":[OSD([sQuery(id+"F2.wireOp",EDGE,"E13.bottom"),sQuery(id+"F2.wireOp",EDGE,"E13.top"),sQuery(id+"F2.wireOp",EDGE,"E13.left"),sQuery(id+"F2.wireOp",EDGE,"E13.right")])],"isStart":false})});
            var Q10;
            Q10=makeQuery(id+"F3.boolean.opBoolean","COPY",FACE,{"derivedFrom":makeQuery(id+"F3.opExtrude","CAP_FACE",FACE,{"disambiguationData":[OSD([sQuery(id+"F2.wireOp",EDGE,"E11.bottom"),sQuery(id+"F2.wireOp",EDGE,"E11.top"),sQuery(id+"F2.wireOp",EDGE,"E11.left"),sQuery(id+"F2.wireOp",EDGE,"E11.right")])],"isStart":false})});
            var Q11;
            Q11=makeQuery(id+"F3.boolean.opBoolean","COPY",FACE,{"derivedFrom":makeQuery(id+"F3.opExtrude","CAP_FACE",FACE,{"disambiguationData":[OSD([sQuery(id+"F2.wireOp",EDGE,"E10.bottom"),sQuery(id+"F2.wireOp",EDGE,"E10.top"),sQuery(id+"F2.wireOp",EDGE,"E10.left"),sQuery(id+"F2.wireOp",EDGE,"E10.right")])],"isStart":false})});
            extrude(context, id + "F45", {"entities" : qUnion([Q0, Q1, Q2, Q3, Q4, Q5, Q6, Q7, Q8, Q9, Q10, Q11]), "depth" : 1 * mm, "offsetDistance" : 25 * mm});
        }
        {
            var Q0;
            Q0=makeQuery(id+"F44.boolean.opBoolean","MERGE",FACE,{"derivedFrom":[makeQuery(id+"F42.boolean.opBoolean","MERGE",FACE,{"derivedFrom":[makeQuery(id+"F9.boolean.opBoolean","MERGE",FACE,{"derivedFrom":[makeQuery(id+"F7.opExtrude","SWEPT_FACE",FACE,{"disambiguationData":[OSD([sQuery(id+"F6.wireOp",EDGE,"E18.top")])]}),makeQuery(id+"F9.opExtrude","SWEPT_FACE",FACE,{"disambiguationData":[OSD([sQuery(id+"F8.wireOp",EDGE,"E19.bottom")])]})]}),makeQuery(id+"F42.opExtrude","SWEPT_FACE",FACE,{"disambiguationData":[OSD([sQuery(id+"F41.wireOp",EDGE,"E40.bottom")])]}),makeQuery(id+"F42.opExtrude","SWEPT_FACE",FACE,{"disambiguationData":[OSD([sQuery(id+"F41.wireOp",EDGE,"E41.bottom")])]}),makeQuery(id+"F42.opExtrude","SWEPT_FACE",FACE,{"disambiguationData":[OSD([sQuery(id+"F41.wireOp",EDGE,"E44.bottom")])]})]}),makeQuery(id+"F44.opExtrude","SWEPT_FACE",FACE,{"disambiguationData":[OSD([sQuery(id+"F43.wireOp",EDGE,"E46.left")])]})]});
            var sketch = newSketch(context, id + "F46", { "sketchPlane" : qUnion([Q0])});
            skLineSegment(sketch, "E47.bottom", {"start": v(305, -174) * mm, "end": v(575, -174) * mm});
            skLineSegment(sketch, "E47.top", {"start": v(305, -264) * mm, "end": v(575, -264) * mm});
            skLineSegment(sketch, "E47.left", {"start": v(290, -189) * mm, "end": v(290, -249) * mm});
            skLineSegment(sketch, "E47.right", {"start": v(590, -189) * mm, "end": v(590, -249) * mm});
            skLineSegment(sketch, "E48.bottom", {"start": v(575, -154) * mm, "end": v(305, -154) * mm});
            skLineSegment(sketch, "E48.top", {"start": v(575, -64) * mm, "end": v(305, -64) * mm});
            skLineSegment(sketch, "E48.left", {"start": v(590, -139) * mm, "end": v(590, -79) * mm});
            skLineSegment(sketch, "E48.right", {"start": v(290, -139) * mm, "end": v(290, -79) * mm});
            skPoint(sketch, "E49.visualSharp", {"position": v(290, -174) * mm});
            skArc(sketch, "E49.filletArc", {"start": v(305, -174) * mm, "mid": v(294.4, -178.4) * mm, "end": v(290, -189) * mm});
            skPoint(sketch, "E50.visualSharp", {"position": v(290, -264) * mm});
            skArc(sketch, "E50.filletArc", {"start": v(290, -249) * mm, "mid": v(294.4, -259.6) * mm, "end": v(305, -264) * mm});
            skPoint(sketch, "E51.visualSharp", {"position": v(590, -174) * mm});
            skArc(sketch, "E51.filletArc", {"start": v(590, -189) * mm, "mid": v(585.6, -178.4) * mm, "end": v(575, -174) * mm});
            skPoint(sketch, "E52.visualSharp", {"position": v(590, -264) * mm});
            skArc(sketch, "E52.filletArc", {"start": v(575, -264) * mm, "mid": v(585.6, -259.6) * mm, "end": v(590, -249) * mm});
            skPoint(sketch, "E53.visualSharp", {"position": v(290, -154) * mm});
            skArc(sketch, "E53.filletArc", {"start": v(290, -139) * mm, "mid": v(294.4, -149.6) * mm, "end": v(305, -154) * mm});
            skPoint(sketch, "E54.visualSharp", {"position": v(290, -64) * mm});
            skArc(sketch, "E54.filletArc", {"start": v(305, -64) * mm, "mid": v(294.4, -68.4) * mm, "end": v(290, -79) * mm});
            skPoint(sketch, "E55.visualSharp", {"position": v(590, -64) * mm});
            skArc(sketch, "E55.filletArc", {"start": v(590, -79) * mm, "mid": v(585.6, -68.4) * mm, "end": v(575, -64) * mm});
            skPoint(sketch, "E56.visualSharp", {"position": v(590, -154) * mm});
            skArc(sketch, "E56.filletArc", {"start": v(575, -154) * mm, "mid": v(585.6, -149.6) * mm, "end": v(590, -139) * mm});
            skLineSegment(sketch, "E57.bottom", {"start": v(375, -99) * mm, "end": v(435, -99) * mm});
            skLineSegment(sketch, "E57.top", {"start": v(375, -119) * mm, "end": v(435, -119) * mm});
            skLineSegment(sketch, "E57.left", {"start": v(375, -99) * mm, "end": v(375, -119) * mm});
            skLineSegment(sketch, "E57.right", {"start": v(435, -99) * mm, "end": v(435, -119) * mm});
            skLineSegment(sketch, "E58.bottom", {"start": v(375, -209) * mm, "end": v(435, -209) * mm});
            skLineSegment(sketch, "E58.top", {"start": v(375, -229) * mm, "end": v(435, -229) * mm});
            skLineSegment(sketch, "E58.left", {"start": v(375, -209) * mm, "end": v(375, -229) * mm});
            skLineSegment(sketch, "E58.right", {"start": v(435, -209) * mm, "end": v(435, -229) * mm});
            skPoint(sketch, "E59.1.0.0", {"position": v(960, -154) * mm});
            skLineSegment(sketch, "E59.1.0.1", {"start": v(1045, -229) * mm, "end": v(1105, -229) * mm});
            skPoint(sketch, "E59.1.0.2", {"position": v(1260, -64) * mm});
            skPoint(sketch, "E59.1.0.3", {"position": v(960, -264) * mm});
            skLineSegment(sketch, "E59.1.0.4", {"start": v(960, -189) * mm, "end": v(960, -249) * mm});
            skLineSegment(sketch, "E59.1.0.5", {"start": v(1045, -209) * mm, "end": v(1105, -209) * mm});
            skLineSegment(sketch, "E59.1.0.6", {"start": v(1045, -119) * mm, "end": v(1105, -119) * mm});
            skLineSegment(sketch, "E59.1.0.7", {"start": v(1260, -139) * mm, "end": v(1260, -79) * mm});
            skPoint(sketch, "E59.1.0.8", {"position": v(1260, -154) * mm});
            skPoint(sketch, "E59.1.0.9", {"position": v(960, -64) * mm});
            skLineSegment(sketch, "E59.1.0.10", {"start": v(1245, -64) * mm, "end": v(975, -64) * mm});
            skLineSegment(sketch, "E59.1.0.11", {"start": v(975, -174) * mm, "end": v(1245, -174) * mm});
            skLineSegment(sketch, "E59.1.0.12", {"start": v(1260, -189) * mm, "end": v(1260, -249) * mm});
            skPoint(sketch, "E59.1.0.13", {"position": v(1260, -264) * mm});
            skLineSegment(sketch, "E59.1.0.14", {"start": v(975, -264) * mm, "end": v(1245, -264) * mm});
            skPoint(sketch, "E59.1.0.15", {"position": v(960, -174) * mm});
            skLineSegment(sketch, "E59.1.0.16", {"start": v(1245, -154) * mm, "end": v(975, -154) * mm});
            skLineSegment(sketch, "E59.1.0.17", {"start": v(960, -139) * mm, "end": v(960, -79) * mm});
            skPoint(sketch, "E59.1.0.18", {"position": v(1260, -174) * mm});
            skLineSegment(sketch, "E59.1.0.19", {"start": v(1045, -99) * mm, "end": v(1105, -99) * mm});
            skLineSegment(sketch, "E59.1.0.20", {"start": v(1045, -209) * mm, "end": v(1045, -229) * mm});
            skArc(sketch, "E59.1.0.21", {"start": v(960, -249) * mm, "mid": v(964.4, -259.6) * mm, "end": v(975, -264) * mm});
            skArc(sketch, "E59.1.0.22", {"start": v(1245, -264) * mm, "mid": v(1255.6, -259.6) * mm, "end": v(1260, -249) * mm});
            skArc(sketch, "E59.1.0.23", {"start": v(1260, -189) * mm, "mid": v(1255.6, -178.4) * mm, "end": v(1245, -174) * mm});
            skArc(sketch, "E59.1.0.24", {"start": v(960, -139) * mm, "mid": v(964.4, -149.6) * mm, "end": v(975, -154) * mm});
            skLineSegment(sketch, "E59.1.0.25", {"start": v(1105, -209) * mm, "end": v(1105, -229) * mm});
            skArc(sketch, "E59.1.0.26", {"start": v(1260, -79) * mm, "mid": v(1255.6, -68.4) * mm, "end": v(1245, -64) * mm});
            skLineSegment(sketch, "E59.1.0.27", {"start": v(1045, -99) * mm, "end": v(1045, -119) * mm});
            skArc(sketch, "E59.1.0.28", {"start": v(975, -174) * mm, "mid": v(964.4, -178.4) * mm, "end": v(960, -189) * mm});
            skArc(sketch, "E59.1.0.29", {"start": v(975, -64) * mm, "mid": v(964.4, -68.4) * mm, "end": v(960, -79) * mm});
            skArc(sketch, "E59.1.0.30", {"start": v(1245, -154) * mm, "mid": v(1255.6, -149.6) * mm, "end": v(1260, -139) * mm});
            skLineSegment(sketch, "E59.1.0.31", {"start": v(1105, -99) * mm, "end": v(1105, -119) * mm});
            skLineSegment(sketch, "E59.direction1", {"start": v(290, -264) * mm, "end": v(960, -264) * mm, "construction": true});
            skSolve(sketch);
        }
        {
            var Q0;
            Q0 = qSketchRegion(id + "F46", true);
            extrude(context, id + "F47", {"entities" : qUnion([Q0]), "depth" : 1.5 * mm, "offsetDistance" : 25 * mm});
        }
        {
            var Q0;
            Q0=makeQuery(id+"F44.boolean.opBoolean","MERGE",FACE,{"derivedFrom":[makeQuery(id+"F42.boolean.opBoolean","MERGE",FACE,{"derivedFrom":[makeQuery(id+"F9.boolean.opBoolean","MERGE",FACE,{"derivedFrom":[makeQuery(id+"F7.opExtrude","SWEPT_FACE",FACE,{"disambiguationData":[OSD([sQuery(id+"F6.wireOp",EDGE,"E18.top")])]}),makeQuery(id+"F9.opExtrude","SWEPT_FACE",FACE,{"disambiguationData":[OSD([sQuery(id+"F8.wireOp",EDGE,"E19.bottom")])]})]}),makeQuery(id+"F42.opExtrude","SWEPT_FACE",FACE,{"disambiguationData":[OSD([sQuery(id+"F41.wireOp",EDGE,"E40.bottom")])]}),makeQuery(id+"F42.opExtrude","SWEPT_FACE",FACE,{"disambiguationData":[OSD([sQuery(id+"F41.wireOp",EDGE,"E41.bottom")])]}),makeQuery(id+"F42.opExtrude","SWEPT_FACE",FACE,{"disambiguationData":[OSD([sQuery(id+"F41.wireOp",EDGE,"E44.bottom")])]})]}),makeQuery(id+"F44.opExtrude","SWEPT_FACE",FACE,{"disambiguationData":[OSD([sQuery(id+"F43.wireOp",EDGE,"E46.left")])]})]});
            var sketch = newSketch(context, id + "F48", { "sketchPlane" : qUnion([Q0])});
            skLineSegment(sketch, "E60.bottom", {"start": v(375, -99) * mm, "end": v(435, -99) * mm});
            skLineSegment(sketch, "E60.top", {"start": v(375, -119) * mm, "end": v(435, -119) * mm});
            skLineSegment(sketch, "E60.left", {"start": v(375, -99) * mm, "end": v(375, -119) * mm});
            skLineSegment(sketch, "E60.right", {"start": v(435, -99) * mm, "end": v(435, -119) * mm});
            skLineSegment(sketch, "E61.bottom", {"start": v(375, -209) * mm, "end": v(435, -209) * mm});
            skLineSegment(sketch, "E61.top", {"start": v(375, -229) * mm, "end": v(435, -229) * mm});
            skLineSegment(sketch, "E61.left", {"start": v(375, -209) * mm, "end": v(375, -229) * mm});
            skLineSegment(sketch, "E61.right", {"start": v(435, -209) * mm, "end": v(435, -229) * mm});
            skLineSegment(sketch, "E62.bottom", {"start": v(1045, -99) * mm, "end": v(1105, -99) * mm});
            skLineSegment(sketch, "E62.top", {"start": v(1045, -119) * mm, "end": v(1105, -119) * mm});
            skLineSegment(sketch, "E62.left", {"start": v(1045, -99) * mm, "end": v(1045, -119) * mm});
            skLineSegment(sketch, "E62.right", {"start": v(1105, -99) * mm, "end": v(1105, -119) * mm});
            skLineSegment(sketch, "E63.bottom", {"start": v(1045, -209) * mm, "end": v(1105, -209) * mm});
            skLineSegment(sketch, "E63.top", {"start": v(1045, -229) * mm, "end": v(1105, -229) * mm});
            skLineSegment(sketch, "E63.left", {"start": v(1045, -209) * mm, "end": v(1045, -229) * mm});
            skLineSegment(sketch, "E63.right", {"start": v(1105, -209) * mm, "end": v(1105, -229) * mm});
            skSolve(sketch);
        }
        {
            var Q0;
            Q0 = qSketchRegion(id + "F48", true);
            extrude(context, id + "F49", {"entities" : qUnion([Q0]), "depth" : 1 * mm, "offsetDistance" : 25 * mm});
        }
        {
            var Q0;
            Q0=makeQuery(id+"F47.opExtrude","CAP_FACE",FACE,{"disambiguationData":[OSD([sQuery(id+"F46.wireOp",EDGE,"E48.bottom"),sQuery(id+"F46.wireOp",EDGE,"E48.top"),sQuery(id+"F46.wireOp",EDGE,"E48.left"),sQuery(id+"F46.wireOp",EDGE,"E48.right"),sQuery(id+"F46.wireOp",EDGE,"E53.filletArc"),sQuery(id+"F46.wireOp",EDGE,"E54.filletArc"),sQuery(id+"F46.wireOp",EDGE,"E55.filletArc"),sQuery(id+"F46.wireOp",EDGE,"E56.filletArc"),sQuery(id+"F46.wireOp",EDGE,"E57.bottom"),sQuery(id+"F46.wireOp",EDGE,"E57.top"),sQuery(id+"F46.wireOp",EDGE,"E57.left"),sQuery(id+"F46.wireOp",EDGE,"E57.right")])],"isStart":false});
            var sketch = newSketch(context, id + "F50", { "sketchPlane" : qUnion([Q0])});
            skCircle(sketch, "E64", {"center": v(340, -109) * mm, "radius": 7.5 * mm});
            skPoint(sketch, "E64.centerSnap0", {"position": v(375, -109) * mm});
            skCircle(sketch, "E65", {"center": v(340, -219) * mm, "radius": 7.5 * mm});
            skCircle(sketch, "E66", {"center": v(1010, -219) * mm, "radius": 7.5 * mm});
            skCircle(sketch, "E67", {"center": v(1010, -109) * mm, "radius": 7.5 * mm});
            skSolve(sketch);
        }
        {
            var Q0;
            Q0 = qSketchRegion(id + "F50", true);
            extrude(context, id + "F51", {"entities" : qUnion([Q0]), "depth" : 2 * mm, "offsetDistance" : 25 * mm});
        }
        {
            var Q0;
            Q0=makeQuery(id+"F47.opExtrude","CAP_FACE",FACE,{"disambiguationData":[OSD([sQuery(id+"F46.wireOp",EDGE,"E48.bottom"),sQuery(id+"F46.wireOp",EDGE,"E48.top"),sQuery(id+"F46.wireOp",EDGE,"E48.left"),sQuery(id+"F46.wireOp",EDGE,"E48.right"),sQuery(id+"F46.wireOp",EDGE,"E53.filletArc"),sQuery(id+"F46.wireOp",EDGE,"E54.filletArc"),sQuery(id+"F46.wireOp",EDGE,"E55.filletArc"),sQuery(id+"F46.wireOp",EDGE,"E56.filletArc"),sQuery(id+"F46.wireOp",EDGE,"E57.bottom"),sQuery(id+"F46.wireOp",EDGE,"E57.top"),sQuery(id+"F46.wireOp",EDGE,"E57.left"),sQuery(id+"F46.wireOp",EDGE,"E57.right")])],"isStart":false});
            var sketch = newSketch(context, id + "F52", { "sketchPlane" : qUnion([Q0])});
            skCircle(sketch, "E68", {"center": v(500, -109) * mm, "radius": 20 * mm});
            skPoint(sketch, "E68.centerSnap0", {"position": v(435, -109) * mm});
            skCircle(sketch, "E69", {"center": v(560, -109) * mm, "radius": 10 * mm});
            skCircle(sketch, "E70.0.1.0", {"center": v(500, -219) * mm, "radius": 20 * mm});
            skCircle(sketch, "E70.0.1.1", {"center": v(560, -219) * mm, "radius": 10 * mm});
            skLineSegment(sketch, "E70.direction2", {"start": v(500, -109) * mm, "end": v(500, -219) * mm, "construction": true});
            skCircle(sketch, "E71.1.0.0", {"center": v(1230, -219) * mm, "radius": 10 * mm});
            skCircle(sketch, "E71.1.0.1", {"center": v(1230, -109) * mm, "radius": 10 * mm});
            skLineSegment(sketch, "E71.1.0.2", {"start": v(1170, -109) * mm, "end": v(1170, -219) * mm, "construction": true});
            skCircle(sketch, "E71.1.0.3", {"center": v(1170, -109) * mm, "radius": 20 * mm});
            skCircle(sketch, "E71.1.0.4", {"center": v(1170, -219) * mm, "radius": 20 * mm});
            skLineSegment(sketch, "E71.direction1", {"start": v(500, -219) * mm, "end": v(1170, -219) * mm, "construction": true});
            skSolve(sketch);
        }
        {
            var Q0;
            Q0=makeQuery(id+"F52.imprint","IMPRINT",FACE,{"disambiguationData":[TD([[makeQuery(id+"F52.imprint","IMPRINT",EDGE,{"derivedFrom":sQuery(id+"F52.wireOp",EDGE,"E68")}),1.0]])]});
            var Q1;
            Q1=makeQuery(id+"F52.imprint","IMPRINT",FACE,{"disambiguationData":[TD([[makeQuery(id+"F52.imprint","IMPRINT",EDGE,{"derivedFrom":sQuery(id+"F52.wireOp",EDGE,"E70.0.1.0")}),1.0]])]});
            var Q2;
            Q2=makeQuery(id+"F52.imprint","IMPRINT",FACE,{"disambiguationData":[TD([[makeQuery(id+"F52.imprint","IMPRINT",EDGE,{"derivedFrom":sQuery(id+"F52.wireOp",EDGE,"c5100197-ee2c-4f06-a532-99fe524eed12.1.0.0")}),1.0]])]});
            var Q3;
            Q3=makeQuery(id+"F52.imprint","IMPRINT",FACE,{"disambiguationData":[TD([[makeQuery(id+"F52.imprint","IMPRINT",EDGE,{"derivedFrom":sQuery(id+"F52.wireOp",EDGE,"c5100197-ee2c-4f06-a532-99fe524eed12.2.0.0")}),1.0]])]});
            var Q4;
            Q4=makeQuery(id+"F52.imprint","IMPRINT",FACE,{"disambiguationData":[TD([[makeQuery(id+"F52.imprint","IMPRINT",EDGE,{"derivedFrom":sQuery(id+"F52.wireOp",EDGE,"E70.1.1.0")}),1.0]])]});
            var Q5;
            Q5=makeQuery(id+"F52.imprint","IMPRINT",FACE,{"disambiguationData":[TD([[makeQuery(id+"F52.imprint","IMPRINT",EDGE,{"derivedFrom":sQuery(id+"F52.wireOp",EDGE,"E70.1.0.0")}),1.0]])]});
            var Q6;
            Q6=makeQuery(id+"F52.imprint","IMPRINT",FACE,{"disambiguationData":[TD([[makeQuery(id+"F52.imprint","IMPRINT",EDGE,{"derivedFrom":sQuery(id+"F52.wireOp",EDGE,"E71.1.0.3")}),1.0]])]});
            var Q7;
            Q7=makeQuery(id+"F52.imprint","IMPRINT",FACE,{"disambiguationData":[TD([[makeQuery(id+"F52.imprint","IMPRINT",EDGE,{"derivedFrom":sQuery(id+"F52.wireOp",EDGE,"E71.1.0.4")}),1.0]])]});
            var Q8;
            Q8=makeQuery(id+"F52.imprint","IMPRINT",FACE,{"disambiguationData":[TD([[makeQuery(id+"F52.imprint","IMPRINT",EDGE,{"derivedFrom":sQuery(id+"F52.wireOp",EDGE,"E71.2.0.3")}),1.0]])]});
            var Q9;
            Q9=makeQuery(id+"F52.imprint","IMPRINT",FACE,{"disambiguationData":[TD([[makeQuery(id+"F52.imprint","IMPRINT",EDGE,{"derivedFrom":sQuery(id+"F52.wireOp",EDGE,"E71.2.0.4")}),1.0]])]});
            extrude(context, id + "F53", {"entities" : qUnion([Q0, Q1, Q2, Q3, Q4, Q5, Q6, Q7, Q8, Q9]), "depth" : 20 * mm, "offsetDistance" : 25 * mm, "hasDraft" : true, "draftAngle" : 10 * degree, "draftPullDirection" : true});
        }
        {
            var Q0;
            Q0=makeQuery(id+"F52.imprint","IMPRINT",FACE,{"disambiguationData":[TD([[makeQuery(id+"F52.imprint","IMPRINT",EDGE,{"derivedFrom":sQuery(id+"F52.wireOp",EDGE,"E69")}),1.0]])]});
            var Q1;
            Q1=makeQuery(id+"F52.imprint","IMPRINT",FACE,{"disambiguationData":[TD([[makeQuery(id+"F52.imprint","IMPRINT",EDGE,{"derivedFrom":sQuery(id+"F52.wireOp",EDGE,"E70.0.1.1")}),1.0]])]});
            var Q2;
            Q2=makeQuery(id+"F52.imprint","IMPRINT",FACE,{"disambiguationData":[TD([[makeQuery(id+"F52.imprint","IMPRINT",EDGE,{"derivedFrom":sQuery(id+"F52.wireOp",EDGE,"c5100197-ee2c-4f06-a532-99fe524eed12.1.0.1")}),1.0]])]});
            var Q3;
            Q3=makeQuery(id+"F52.imprint","IMPRINT",FACE,{"disambiguationData":[TD([[makeQuery(id+"F52.imprint","IMPRINT",EDGE,{"derivedFrom":sQuery(id+"F52.wireOp",EDGE,"c5100197-ee2c-4f06-a532-99fe524eed12.2.0.1")}),1.0]])]});
            var Q4;
            Q4=makeQuery(id+"F52.imprint","IMPRINT",FACE,{"disambiguationData":[TD([[makeQuery(id+"F52.imprint","IMPRINT",EDGE,{"derivedFrom":sQuery(id+"F52.wireOp",EDGE,"E70.1.1.1")}),1.0]])]});
            var Q5;
            Q5=makeQuery(id+"F52.imprint","IMPRINT",FACE,{"disambiguationData":[TD([[makeQuery(id+"F52.imprint","IMPRINT",EDGE,{"derivedFrom":sQuery(id+"F52.wireOp",EDGE,"E70.1.0.1")}),1.0]])]});
            var Q6;
            Q6=makeQuery(id+"F52.imprint","IMPRINT",FACE,{"disambiguationData":[TD([[makeQuery(id+"F52.imprint","IMPRINT",EDGE,{"derivedFrom":sQuery(id+"F52.wireOp",EDGE,"E71.1.0.1")}),1.0]])]});
            var Q7;
            Q7=makeQuery(id+"F52.imprint","IMPRINT",FACE,{"disambiguationData":[TD([[makeQuery(id+"F52.imprint","IMPRINT",EDGE,{"derivedFrom":sQuery(id+"F52.wireOp",EDGE,"E71.1.0.0")}),1.0]])]});
            var Q8;
            Q8=makeQuery(id+"F52.imprint","IMPRINT",FACE,{"disambiguationData":[TD([[makeQuery(id+"F52.imprint","IMPRINT",EDGE,{"derivedFrom":sQuery(id+"F52.wireOp",EDGE,"E71.2.0.1")}),1.0]])]});
            var Q9;
            Q9=makeQuery(id+"F52.imprint","IMPRINT",FACE,{"disambiguationData":[TD([[makeQuery(id+"F52.imprint","IMPRINT",EDGE,{"derivedFrom":sQuery(id+"F52.wireOp",EDGE,"E71.2.0.0")}),1.0]])]});
            extrude(context, id + "F54", {"entities" : qUnion([Q0, Q1, Q2, Q3, Q4, Q5, Q6, Q7, Q8, Q9]), "depth" : 10 * mm, "offsetDistance" : 25 * mm, "hasDraft" : true, "draftAngle" : 5 * degree, "draftPullDirection" : true});
        }
    });
